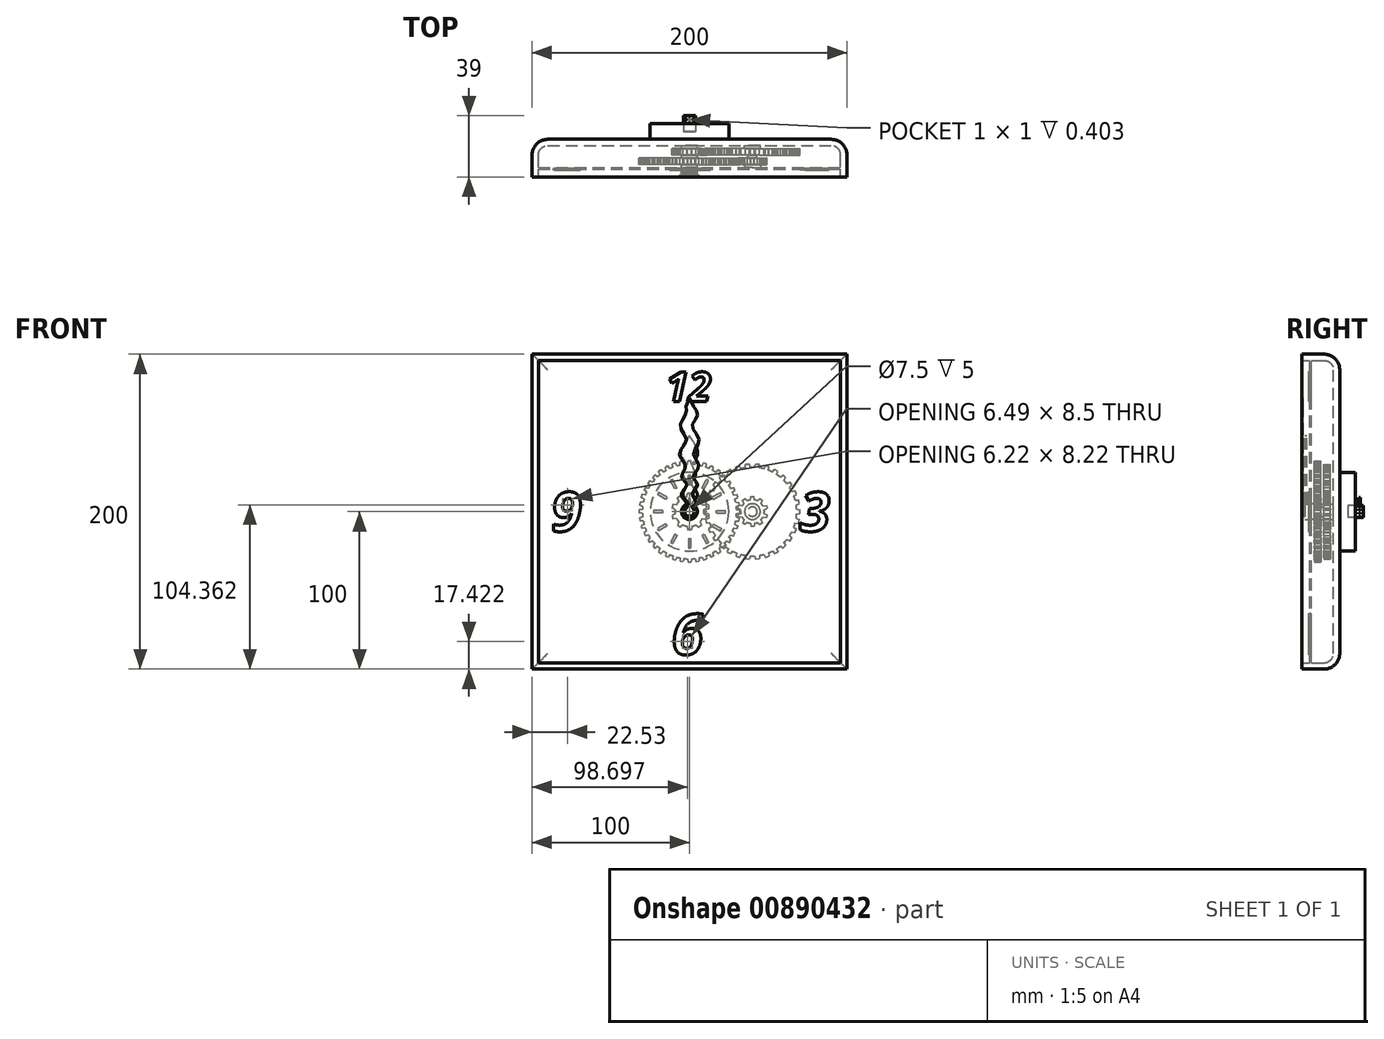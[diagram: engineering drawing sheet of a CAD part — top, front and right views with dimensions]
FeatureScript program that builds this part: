
annotation { "Feature Type Name" : "Feature", "Feature Type Description" : "" }
export const myFeature = defineFeature(function(context is Context, id is Id, definition is map)
    precondition{}
    {
        {
            var Q0;
            Q0=qCreatedBy(makeId("Front.planeOp"),FACE);
            var sketch = newSketch(context, id + "F0", { "sketchPlane" : qUnion([Q0])});
            skLineSegment(sketch, "E0.bottom", {"start": v(-100, -100) * mm, "end": v(100, -100) * mm});
            skLineSegment(sketch, "E0.top", {"start": v(-100, 100) * mm, "end": v(100, 100) * mm});
            skLineSegment(sketch, "E0.left", {"start": v(-100, -100) * mm, "end": v(-100, 100) * mm});
            skLineSegment(sketch, "E0.right", {"start": v(100, -100) * mm, "end": v(100, 100) * mm});
            skPoint(sketch, "E0.middle", {"position": v(0, 0) * mm});
            skSolve(sketch);
        }
        {
            var Q0;
            Q0 = qSketchRegion(id + "F0", true);
            extrude(context, id + "F1", {"entities" : qUnion([Q0]), "depth" : 24 * mm, "offsetDistance" : 25 * mm});
        }
        {
            var Q0;
            Q0=makeQuery(id+"F1.opExtrude","CAP_EDGE",EDGE,{"disambiguationData":[OSD([sQuery(id+"F0.wireOp",EDGE,"E0.top")])],"isStart":true});
            var Q1;
            Q1=makeQuery(id+"F1.opExtrude","CAP_EDGE",EDGE,{"disambiguationData":[OSD([sQuery(id+"F0.wireOp",EDGE,"E0.left")])],"isStart":true});
            var Q2;
            Q2=makeQuery(id+"F1.opExtrude","CAP_EDGE",EDGE,{"disambiguationData":[OSD([sQuery(id+"F0.wireOp",EDGE,"E0.bottom")])],"isStart":true});
            var Q3;
            Q3=makeQuery(id+"F1.opExtrude","CAP_EDGE",EDGE,{"disambiguationData":[OSD([sQuery(id+"F0.wireOp",EDGE,"E0.right")])],"isStart":true});
            fillet(context, id + "F2", {"entities" : qUnion([Q0, Q1, Q2, Q3]), "radius" : 10 * mm, "tangentPropagation" : true, "allowEdgeOverflow" : false});
        }
        {
            var Q0;
            Q0=makeQuery(id+"F1.opExtrude","CAP_FACE",FACE,{"disambiguationData":[OSD([sQuery(id+"F0.wireOp",EDGE,"E0.bottom"),sQuery(id+"F0.wireOp",EDGE,"E0.top"),sQuery(id+"F0.wireOp",EDGE,"E0.left"),sQuery(id+"F0.wireOp",EDGE,"E0.right")])],"isStart":false});
            shell(context, id + "F3", {"entities" : qUnion([Q0]), "thickness" : 4 * mm});
        }
        {
            var Q0;
            Q0=makeQuery(id+"F3.opShell","OFFSET_FACE",FACE,{"disambiguationData":[OSD([sQuery(id+"F0.wireOp",EDGE,"E0.bottom"),sQuery(id+"F0.wireOp",EDGE,"E0.top"),sQuery(id+"F0.wireOp",EDGE,"E0.left"),sQuery(id+"F0.wireOp",EDGE,"E0.right")])]});
            var sketch = newSketch(context, id + "F4", { "sketchPlane" : qUnion([Q0])});
            skCircle(sketch, "E1", {"center": v(0, 0) * mm, "radius": 3 * mm});
            skCircle(sketch, "E2", {"center": v(0, 0) * mm, "radius": 5 * mm});
            skCircle(sketch, "E3", {"center": v(40, 0) * mm, "radius": 3 * mm});
            skCircle(sketch, "E4", {"center": v(40, 0) * mm, "radius": 5 * mm});
            skSolve(sketch);
        }
        {
            var Q0;
            Q0 = qSketchRegion(id + "F4", true);
            extrude(context, id + "F5", {"entities" : qUnion([Q0]), "operationType" : NewBodyOperationType.ADD, "depth" : 2 * mm, "offsetDistance" : 25 * mm});
        }
        {
            var Q0;
            Q0=makeQuery(id+"F5.boolean.opBoolean","SPLIT",FACE,{"disambiguationData":[TD([makeQuery(id+"F5.opExtrude","SWEPT_FACE",FACE,{"disambiguationData":[OSD([sQuery(id+"F4.wireOp",EDGE,"E1")])]})])],"derivedFrom":makeQuery(id+"F3.opShell","OFFSET_FACE",FACE,{"disambiguationData":[OSD([sQuery(id+"F0.wireOp",EDGE,"E0.bottom"),sQuery(id+"F0.wireOp",EDGE,"E0.top"),sQuery(id+"F0.wireOp",EDGE,"E0.left"),sQuery(id+"F0.wireOp",EDGE,"E0.right")])]})});
            extrude(context, id + "F6", {"entities" : qUnion([Q0]), "depth" : 19 * mm, "offsetDistance" : 25 * mm});
        }
        {
            var Q0;
            Q0=makeQuery(id+"F5.boolean.opBoolean","SPLIT",FACE,{"disambiguationData":[TD([makeQuery(id+"F5.opExtrude","SWEPT_FACE",FACE,{"disambiguationData":[OSD([sQuery(id+"F4.wireOp",EDGE,"E3")])]})])],"derivedFrom":makeQuery(id+"F3.opShell","OFFSET_FACE",FACE,{"disambiguationData":[OSD([sQuery(id+"F0.wireOp",EDGE,"E0.bottom"),sQuery(id+"F0.wireOp",EDGE,"E0.top"),sQuery(id+"F0.wireOp",EDGE,"E0.left"),sQuery(id+"F0.wireOp",EDGE,"E0.right")])]})});
            extrude(context, id + "F7", {"entities" : qUnion([Q0]), "depth" : 8 * mm, "offsetDistance" : 25 * mm});
        }
        {
            var Q0;
            Q0=makeQuery(id+"F5.opExtrude","CAP_FACE",FACE,{"disambiguationData":[OSD([sQuery(id+"F4.wireOp",EDGE,"E1"),sQuery(id+"F4.wireOp",EDGE,"E2")])],"isStart":false});
            var sketch = newSketch(context, id + "F8", { "sketchPlane" : qUnion([Q0])});
            skCircle(sketch, "E5", {"center": v(0, 0) * mm, "radius": 9.38 * mm});
            skLineSegment(sketch, "E6", {"start": v(1.55, 9.25) * mm, "end": v(1.18, 11.38) * mm});
            skLineSegment(sketch, "E7", {"start": v(1.18, 11.38) * mm, "end": v(0, 11.38) * mm});
            skLineSegment(sketch, "E8.MirrorCS", {"start": v(-1.18, 11.38) * mm, "end": v(0, 11.38) * mm});
            skLineSegment(sketch, "E9.MirrorCS", {"start": v(-1.55, 9.25) * mm, "end": v(-1.18, 11.38) * mm});
            skLineSegment(sketch, "E10.1.0", {"start": v(-4.18, 8.4) * mm, "end": v(-5.73, 9.9) * mm});
            skLineSegment(sketch, "E10.1.1", {"start": v(-5.73, 9.9) * mm, "end": v(-6.69, 9.2) * mm});
            skLineSegment(sketch, "E10.1.2", {"start": v(-7.64, 8.51) * mm, "end": v(-6.69, 9.2) * mm});
            skLineSegment(sketch, "E10.1.3", {"start": v(-6.7, 6.57) * mm, "end": v(-7.64, 8.51) * mm});
            skLineSegment(sketch, "E10.2.0", {"start": v(-8.31, 4.33) * mm, "end": v(-10.45, 4.64) * mm});
            skLineSegment(sketch, "E10.2.1", {"start": v(-10.45, 4.64) * mm, "end": v(-10.82, 3.52) * mm});
            skLineSegment(sketch, "E10.2.2", {"start": v(-11.18, 2.4) * mm, "end": v(-10.82, 3.52) * mm});
            skLineSegment(sketch, "E10.2.3", {"start": v(-9.27, 1.38) * mm, "end": v(-11.18, 2.4) * mm});
            skLineSegment(sketch, "E11.1.3.0", {"start": v(-9.27, -1.38) * mm, "end": v(-11.18, -2.4) * mm});
            skLineSegment(sketch, "E11.3.3.0", {"start": v(-11.18, -2.4) * mm, "end": v(-10.82, -3.52) * mm});
            skLineSegment(sketch, "E11.6.3.0", {"start": v(-10.45, -4.64) * mm, "end": v(-10.82, -3.52) * mm});
            skLineSegment(sketch, "E11.9.3.0", {"start": v(-8.31, -4.33) * mm, "end": v(-10.45, -4.64) * mm});
            skLineSegment(sketch, "E11.1.4.0", {"start": v(-6.7, -6.57) * mm, "end": v(-7.64, -8.51) * mm});
            skLineSegment(sketch, "E11.3.4.0", {"start": v(-7.64, -8.51) * mm, "end": v(-6.69, -9.2) * mm});
            skLineSegment(sketch, "E11.6.4.0", {"start": v(-5.73, -9.9) * mm, "end": v(-6.69, -9.2) * mm});
            skLineSegment(sketch, "E11.9.4.0", {"start": v(-4.18, -8.4) * mm, "end": v(-5.73, -9.9) * mm});
            skLineSegment(sketch, "E11.1.5.0", {"start": v(-1.55, -9.25) * mm, "end": v(-1.18, -11.38) * mm});
            skLineSegment(sketch, "E11.3.5.0", {"start": v(-1.18, -11.38) * mm, "end": v(0, -11.38) * mm});
            skLineSegment(sketch, "E11.6.5.0", {"start": v(1.18, -11.38) * mm, "end": v(0, -11.38) * mm});
            skLineSegment(sketch, "E11.9.5.0", {"start": v(1.55, -9.25) * mm, "end": v(1.18, -11.38) * mm});
            skLineSegment(sketch, "E11.1.6.0", {"start": v(4.18, -8.4) * mm, "end": v(5.73, -9.9) * mm});
            skLineSegment(sketch, "E11.3.6.0", {"start": v(5.73, -9.9) * mm, "end": v(6.69, -9.2) * mm});
            skLineSegment(sketch, "E11.6.6.0", {"start": v(7.64, -8.51) * mm, "end": v(6.69, -9.2) * mm});
            skLineSegment(sketch, "E11.9.6.0", {"start": v(6.7, -6.57) * mm, "end": v(7.64, -8.51) * mm});
            skLineSegment(sketch, "E11.1.7.0", {"start": v(8.31, -4.33) * mm, "end": v(10.45, -4.64) * mm});
            skLineSegment(sketch, "E11.3.7.0", {"start": v(10.45, -4.64) * mm, "end": v(10.82, -3.52) * mm});
            skLineSegment(sketch, "E11.6.7.0", {"start": v(11.18, -2.4) * mm, "end": v(10.82, -3.52) * mm});
            skLineSegment(sketch, "E11.9.7.0", {"start": v(9.27, -1.38) * mm, "end": v(11.18, -2.4) * mm});
            skLineSegment(sketch, "E11.1.8.0", {"start": v(9.27, 1.38) * mm, "end": v(11.18, 2.4) * mm});
            skLineSegment(sketch, "E11.3.8.0", {"start": v(11.18, 2.4) * mm, "end": v(10.82, 3.52) * mm});
            skLineSegment(sketch, "E11.6.8.0", {"start": v(10.45, 4.64) * mm, "end": v(10.82, 3.52) * mm});
            skLineSegment(sketch, "E11.9.8.0", {"start": v(8.31, 4.33) * mm, "end": v(10.45, 4.64) * mm});
            skLineSegment(sketch, "E11.1.9.0", {"start": v(6.7, 6.57) * mm, "end": v(7.64, 8.51) * mm});
            skLineSegment(sketch, "E11.3.9.0", {"start": v(7.64, 8.51) * mm, "end": v(6.69, 9.2) * mm});
            skLineSegment(sketch, "E11.6.9.0", {"start": v(5.73, 9.9) * mm, "end": v(6.69, 9.2) * mm});
            skLineSegment(sketch, "E11.9.9.0", {"start": v(4.18, 8.4) * mm, "end": v(5.73, 9.9) * mm});
            skSolve(sketch);
        }
        {
            var Q0;
            Q0 = qSketchRegion(id + "F8", true);
            extrude(context, id + "F9", {"entities" : qUnion([Q0]), "operationType" : NewBodyOperationType.ADD, "depth" : 4 * mm, "offsetDistance" : 25 * mm});
        }
        {
            var Q0;
            Q0=makeQuery(id+"F5.opExtrude","CAP_FACE",FACE,{"disambiguationData":[OSD([sQuery(id+"F4.wireOp",EDGE,"E3"),sQuery(id+"F4.wireOp",EDGE,"E4")])],"isStart":false});
            var sketch = newSketch(context, id + "F10", { "sketchPlane" : qUnion([Q0])});
            skCircle(sketch, "E12", {"center": v(40, 0) * mm, "radius": 28.12 * mm});
            skLineSegment(sketch, "E13", {"start": v(11.92, 1.54) * mm, "end": v(9.88, 1.18) * mm});
            skLineSegment(sketch, "E14", {"start": v(9.88, 1.18) * mm, "end": v(9.88, 0) * mm});
            skLineSegment(sketch, "E15.MirrorCS", {"start": v(9.88, -1.18) * mm, "end": v(9.88, 0) * mm});
            skLineSegment(sketch, "E16.MirrorCS", {"start": v(11.92, -1.54) * mm, "end": v(9.88, -1.18) * mm});
            skLineSegment(sketch, "E17.1.0", {"start": v(12.21, -4.33) * mm, "end": v(10.29, -5.11) * mm});
            skLineSegment(sketch, "E17.1.1", {"start": v(10.29, -5.11) * mm, "end": v(10.53, -6.26) * mm});
            skLineSegment(sketch, "E17.1.2", {"start": v(10.78, -7.42) * mm, "end": v(10.53, -6.26) * mm});
            skLineSegment(sketch, "E17.1.3", {"start": v(12.85, -7.34) * mm, "end": v(10.78, -7.42) * mm});
            skLineSegment(sketch, "E17.2.0", {"start": v(13.72, -10.02) * mm, "end": v(12, -11.18) * mm});
            skLineSegment(sketch, "E17.2.1", {"start": v(12, -11.18) * mm, "end": v(12.48, -12.25) * mm});
            skLineSegment(sketch, "E17.2.2", {"start": v(12.96, -13.33) * mm, "end": v(12.48, -12.25) * mm});
            skLineSegment(sketch, "E17.2.3", {"start": v(14.97, -12.83) * mm, "end": v(12.96, -13.33) * mm});
            skLineSegment(sketch, "E18.2.3.0", {"start": v(16.38, -15.26) * mm, "end": v(14.94, -16.75) * mm});
            skLineSegment(sketch, "E18.3.3.0", {"start": v(14.94, -16.75) * mm, "end": v(15.63, -17.7) * mm});
            skLineSegment(sketch, "E18.6.3.0", {"start": v(16.32, -18.66) * mm, "end": v(15.63, -17.7) * mm});
            skLineSegment(sketch, "E18.9.3.0", {"start": v(18.18, -17.75) * mm, "end": v(16.32, -18.66) * mm});
            skLineSegment(sketch, "E18.2.4.0", {"start": v(20.07, -19.84) * mm, "end": v(18.97, -21.6) * mm});
            skLineSegment(sketch, "E18.3.4.0", {"start": v(18.97, -21.6) * mm, "end": v(19.84, -22.39) * mm});
            skLineSegment(sketch, "E18.6.4.0", {"start": v(20.72, -23.18) * mm, "end": v(19.84, -22.39) * mm});
            skLineSegment(sketch, "E18.9.4.0", {"start": v(22.35, -21.9) * mm, "end": v(20.72, -23.18) * mm});
            skLineSegment(sketch, "E18.2.5.0", {"start": v(24.63, -23.55) * mm, "end": v(23.92, -25.5) * mm});
            skLineSegment(sketch, "E18.3.5.0", {"start": v(23.92, -25.5) * mm, "end": v(24.94, -26.09) * mm});
            skLineSegment(sketch, "E18.6.5.0", {"start": v(25.96, -26.68) * mm, "end": v(24.94, -26.09) * mm});
            skLineSegment(sketch, "E18.9.5.0", {"start": v(27.3, -25.09) * mm, "end": v(25.96, -26.68) * mm});
            skLineSegment(sketch, "E18.2.6.0", {"start": v(29.86, -26.23) * mm, "end": v(29.57, -28.29) * mm});
            skLineSegment(sketch, "E18.3.6.0", {"start": v(29.57, -28.29) * mm, "end": v(30.7, -28.65) * mm});
            skLineSegment(sketch, "E18.6.6.0", {"start": v(31.81, -29.01) * mm, "end": v(30.7, -28.65) * mm});
            skLineSegment(sketch, "E18.9.6.0", {"start": v(32.78, -27.18) * mm, "end": v(31.81, -29.01) * mm});
            skLineSegment(sketch, "E18.2.7.0", {"start": v(35.53, -27.77) * mm, "end": v(35.68, -29.84) * mm});
            skLineSegment(sketch, "E18.3.7.0", {"start": v(35.68, -29.84) * mm, "end": v(36.85, -29.96) * mm});
            skLineSegment(sketch, "E18.6.7.0", {"start": v(38.02, -30.08) * mm, "end": v(36.85, -29.96) * mm});
            skLineSegment(sketch, "E18.9.7.0", {"start": v(38.6, -28.09) * mm, "end": v(38.02, -30.08) * mm});
            skLineSegment(sketch, "E18.2.8.0", {"start": v(41.4, -28.09) * mm, "end": v(41.98, -30.08) * mm});
            skLineSegment(sketch, "E18.3.8.0", {"start": v(41.98, -30.08) * mm, "end": v(43.15, -29.96) * mm});
            skLineSegment(sketch, "E18.6.8.0", {"start": v(44.32, -29.84) * mm, "end": v(43.15, -29.96) * mm});
            skLineSegment(sketch, "E18.9.8.0", {"start": v(44.47, -27.77) * mm, "end": v(44.32, -29.84) * mm});
            skLineSegment(sketch, "E18.2.9.0", {"start": v(47.22, -27.18) * mm, "end": v(48.19, -29.01) * mm});
            skLineSegment(sketch, "E18.3.9.0", {"start": v(48.19, -29.01) * mm, "end": v(49.3, -28.65) * mm});
            skLineSegment(sketch, "E18.6.9.0", {"start": v(50.43, -28.29) * mm, "end": v(49.3, -28.65) * mm});
            skLineSegment(sketch, "E18.9.9.0", {"start": v(50.14, -26.23) * mm, "end": v(50.43, -28.29) * mm});
            skLineSegment(sketch, "E18.2.10.0", {"start": v(52.7, -25.09) * mm, "end": v(54.04, -26.68) * mm});
            skLineSegment(sketch, "E18.3.10.0", {"start": v(54.04, -26.68) * mm, "end": v(55.06, -26.09) * mm});
            skLineSegment(sketch, "E18.6.10.0", {"start": v(56.08, -25.5) * mm, "end": v(55.06, -26.09) * mm});
            skLineSegment(sketch, "E18.9.10.0", {"start": v(55.37, -23.55) * mm, "end": v(56.08, -25.5) * mm});
            skLineSegment(sketch, "E18.2.11.0", {"start": v(57.65, -21.9) * mm, "end": v(59.28, -23.18) * mm});
            skLineSegment(sketch, "E18.3.11.0", {"start": v(59.28, -23.18) * mm, "end": v(60.16, -22.39) * mm});
            skLineSegment(sketch, "E18.6.11.0", {"start": v(61.03, -21.6) * mm, "end": v(60.16, -22.39) * mm});
            skLineSegment(sketch, "E18.9.11.0", {"start": v(59.93, -19.84) * mm, "end": v(61.03, -21.6) * mm});
            skLineSegment(sketch, "E18.2.12.0", {"start": v(61.82, -17.75) * mm, "end": v(63.68, -18.66) * mm});
            skLineSegment(sketch, "E18.3.12.0", {"start": v(63.68, -18.66) * mm, "end": v(64.37, -17.7) * mm});
            skLineSegment(sketch, "E18.6.12.0", {"start": v(65.06, -16.75) * mm, "end": v(64.37, -17.7) * mm});
            skLineSegment(sketch, "E18.9.12.0", {"start": v(63.62, -15.26) * mm, "end": v(65.06, -16.75) * mm});
            skLineSegment(sketch, "E18.2.13.0", {"start": v(65.03, -12.83) * mm, "end": v(67.04, -13.33) * mm});
            skLineSegment(sketch, "E18.3.13.0", {"start": v(67.04, -13.33) * mm, "end": v(67.52, -12.25) * mm});
            skLineSegment(sketch, "E18.6.13.0", {"start": v(68, -11.18) * mm, "end": v(67.52, -12.25) * mm});
            skLineSegment(sketch, "E18.9.13.0", {"start": v(66.28, -10.02) * mm, "end": v(68, -11.18) * mm});
            skLineSegment(sketch, "E18.2.14.0", {"start": v(67.15, -7.34) * mm, "end": v(69.22, -7.42) * mm});
            skLineSegment(sketch, "E18.3.14.0", {"start": v(69.22, -7.42) * mm, "end": v(69.47, -6.26) * mm});
            skLineSegment(sketch, "E18.6.14.0", {"start": v(69.71, -5.11) * mm, "end": v(69.47, -6.26) * mm});
            skLineSegment(sketch, "E18.9.14.0", {"start": v(67.79, -4.33) * mm, "end": v(69.71, -5.11) * mm});
            skLineSegment(sketch, "E18.2.15.0", {"start": v(68.08, -1.54) * mm, "end": v(70.12, -1.18) * mm});
            skLineSegment(sketch, "E18.3.15.0", {"start": v(70.12, -1.18) * mm, "end": v(70.12, 0) * mm});
            skLineSegment(sketch, "E18.6.15.0", {"start": v(70.12, 1.18) * mm, "end": v(70.12, 0) * mm});
            skLineSegment(sketch, "E18.9.15.0", {"start": v(68.08, 1.54) * mm, "end": v(70.12, 1.18) * mm});
            skLineSegment(sketch, "E18.2.16.0", {"start": v(67.79, 4.33) * mm, "end": v(69.71, 5.11) * mm});
            skLineSegment(sketch, "E18.3.16.0", {"start": v(69.71, 5.11) * mm, "end": v(69.47, 6.26) * mm});
            skLineSegment(sketch, "E18.6.16.0", {"start": v(69.22, 7.42) * mm, "end": v(69.47, 6.26) * mm});
            skLineSegment(sketch, "E18.9.16.0", {"start": v(67.15, 7.34) * mm, "end": v(69.22, 7.42) * mm});
            skLineSegment(sketch, "E18.2.17.0", {"start": v(66.28, 10.02) * mm, "end": v(68, 11.18) * mm});
            skLineSegment(sketch, "E18.3.17.0", {"start": v(68, 11.18) * mm, "end": v(67.52, 12.25) * mm});
            skLineSegment(sketch, "E18.6.17.0", {"start": v(67.04, 13.33) * mm, "end": v(67.52, 12.25) * mm});
            skLineSegment(sketch, "E18.9.17.0", {"start": v(65.03, 12.83) * mm, "end": v(67.04, 13.33) * mm});
            skLineSegment(sketch, "E18.2.18.0", {"start": v(63.62, 15.26) * mm, "end": v(65.06, 16.75) * mm});
            skLineSegment(sketch, "E18.3.18.0", {"start": v(65.06, 16.75) * mm, "end": v(64.37, 17.7) * mm});
            skLineSegment(sketch, "E18.6.18.0", {"start": v(63.68, 18.66) * mm, "end": v(64.37, 17.7) * mm});
            skLineSegment(sketch, "E18.9.18.0", {"start": v(61.82, 17.75) * mm, "end": v(63.68, 18.66) * mm});
            skLineSegment(sketch, "E18.2.19.0", {"start": v(59.93, 19.84) * mm, "end": v(61.03, 21.6) * mm});
            skLineSegment(sketch, "E18.3.19.0", {"start": v(61.03, 21.6) * mm, "end": v(60.16, 22.39) * mm});
            skLineSegment(sketch, "E18.6.19.0", {"start": v(59.28, 23.18) * mm, "end": v(60.16, 22.39) * mm});
            skLineSegment(sketch, "E18.9.19.0", {"start": v(57.65, 21.9) * mm, "end": v(59.28, 23.18) * mm});
            skLineSegment(sketch, "E18.2.20.0", {"start": v(55.37, 23.55) * mm, "end": v(56.08, 25.5) * mm});
            skLineSegment(sketch, "E18.3.20.0", {"start": v(56.08, 25.5) * mm, "end": v(55.06, 26.09) * mm});
            skLineSegment(sketch, "E18.6.20.0", {"start": v(54.04, 26.68) * mm, "end": v(55.06, 26.09) * mm});
            skLineSegment(sketch, "E18.9.20.0", {"start": v(52.7, 25.09) * mm, "end": v(54.04, 26.68) * mm});
            skLineSegment(sketch, "E18.2.21.0", {"start": v(50.14, 26.23) * mm, "end": v(50.43, 28.29) * mm});
            skLineSegment(sketch, "E18.3.21.0", {"start": v(50.43, 28.29) * mm, "end": v(49.3, 28.65) * mm});
            skLineSegment(sketch, "E18.6.21.0", {"start": v(48.19, 29.01) * mm, "end": v(49.3, 28.65) * mm});
            skLineSegment(sketch, "E18.9.21.0", {"start": v(47.22, 27.18) * mm, "end": v(48.19, 29.01) * mm});
            skLineSegment(sketch, "E18.2.22.0", {"start": v(44.47, 27.77) * mm, "end": v(44.32, 29.84) * mm});
            skLineSegment(sketch, "E18.3.22.0", {"start": v(44.32, 29.84) * mm, "end": v(43.15, 29.96) * mm});
            skLineSegment(sketch, "E18.6.22.0", {"start": v(41.98, 30.08) * mm, "end": v(43.15, 29.96) * mm});
            skLineSegment(sketch, "E18.9.22.0", {"start": v(41.4, 28.09) * mm, "end": v(41.98, 30.08) * mm});
            skLineSegment(sketch, "E18.2.23.0", {"start": v(38.6, 28.09) * mm, "end": v(38.02, 30.08) * mm});
            skLineSegment(sketch, "E18.3.23.0", {"start": v(38.02, 30.08) * mm, "end": v(36.85, 29.96) * mm});
            skLineSegment(sketch, "E18.6.23.0", {"start": v(35.68, 29.84) * mm, "end": v(36.85, 29.96) * mm});
            skLineSegment(sketch, "E18.9.23.0", {"start": v(35.53, 27.77) * mm, "end": v(35.68, 29.84) * mm});
            skLineSegment(sketch, "E18.2.24.0", {"start": v(32.78, 27.18) * mm, "end": v(31.81, 29.01) * mm});
            skLineSegment(sketch, "E18.3.24.0", {"start": v(31.81, 29.01) * mm, "end": v(30.7, 28.65) * mm});
            skLineSegment(sketch, "E18.6.24.0", {"start": v(29.57, 28.29) * mm, "end": v(30.7, 28.65) * mm});
            skLineSegment(sketch, "E18.9.24.0", {"start": v(29.86, 26.23) * mm, "end": v(29.57, 28.29) * mm});
            skLineSegment(sketch, "E18.2.25.0", {"start": v(27.3, 25.09) * mm, "end": v(25.96, 26.68) * mm});
            skLineSegment(sketch, "E18.3.25.0", {"start": v(25.96, 26.68) * mm, "end": v(24.94, 26.09) * mm});
            skLineSegment(sketch, "E18.6.25.0", {"start": v(23.92, 25.5) * mm, "end": v(24.94, 26.09) * mm});
            skLineSegment(sketch, "E18.9.25.0", {"start": v(24.63, 23.55) * mm, "end": v(23.92, 25.5) * mm});
            skLineSegment(sketch, "E18.2.26.0", {"start": v(22.35, 21.9) * mm, "end": v(20.72, 23.18) * mm});
            skLineSegment(sketch, "E18.3.26.0", {"start": v(20.72, 23.18) * mm, "end": v(19.84, 22.39) * mm});
            skLineSegment(sketch, "E18.6.26.0", {"start": v(18.97, 21.6) * mm, "end": v(19.84, 22.39) * mm});
            skLineSegment(sketch, "E18.9.26.0", {"start": v(20.07, 19.84) * mm, "end": v(18.97, 21.6) * mm});
            skLineSegment(sketch, "E18.2.27.0", {"start": v(18.18, 17.75) * mm, "end": v(16.32, 18.66) * mm});
            skLineSegment(sketch, "E18.3.27.0", {"start": v(16.32, 18.66) * mm, "end": v(15.63, 17.7) * mm});
            skLineSegment(sketch, "E18.6.27.0", {"start": v(14.94, 16.75) * mm, "end": v(15.63, 17.7) * mm});
            skLineSegment(sketch, "E18.9.27.0", {"start": v(16.38, 15.26) * mm, "end": v(14.94, 16.75) * mm});
            skLineSegment(sketch, "E18.2.28.0", {"start": v(14.97, 12.83) * mm, "end": v(12.96, 13.33) * mm});
            skLineSegment(sketch, "E18.3.28.0", {"start": v(12.96, 13.33) * mm, "end": v(12.48, 12.25) * mm});
            skLineSegment(sketch, "E18.6.28.0", {"start": v(12, 11.18) * mm, "end": v(12.48, 12.25) * mm});
            skLineSegment(sketch, "E18.9.28.0", {"start": v(13.72, 10.02) * mm, "end": v(12, 11.18) * mm});
            skLineSegment(sketch, "E18.2.29.0", {"start": v(12.85, 7.34) * mm, "end": v(10.78, 7.42) * mm});
            skLineSegment(sketch, "E18.3.29.0", {"start": v(10.78, 7.42) * mm, "end": v(10.53, 6.26) * mm});
            skLineSegment(sketch, "E18.6.29.0", {"start": v(10.29, 5.11) * mm, "end": v(10.53, 6.26) * mm});
            skLineSegment(sketch, "E18.9.29.0", {"start": v(12.21, 4.33) * mm, "end": v(10.29, 5.11) * mm});
            skSolve(sketch);
        }
        {
            var Q0;
            Q0 = qSketchRegion(id + "F10", true);
            extrude(context, id + "F11", {"entities" : qUnion([Q0]), "operationType" : NewBodyOperationType.ADD, "depth" : 4 * mm, "offsetDistance" : 25 * mm});
        }
        {
            var Q0;
            Q0=makeQuery(id+"F9.opExtrude","CAP_FACE",FACE,{"disambiguationData":[OSD([sQuery(id+"F8.wireOp",EDGE,"E5"),sQuery(id+"F8.wireOp",EDGE,"E6"),sQuery(id+"F8.wireOp",EDGE,"E7"),sQuery(id+"F8.wireOp",EDGE,"E8.MirrorCS"),sQuery(id+"F8.wireOp",EDGE,"E9.MirrorCS"),sQuery(id+"F8.wireOp",EDGE,"E10.1.0"),sQuery(id+"F8.wireOp",EDGE,"E10.1.1"),sQuery(id+"F8.wireOp",EDGE,"E10.1.2"),sQuery(id+"F8.wireOp",EDGE,"E10.1.3"),sQuery(id+"F8.wireOp",EDGE,"E10.2.0"),sQuery(id+"F8.wireOp",EDGE,"E10.2.1"),sQuery(id+"F8.wireOp",EDGE,"E10.2.2"),sQuery(id+"F8.wireOp",EDGE,"E10.2.3"),sQuery(id+"F8.wireOp",EDGE,"E11.1.3.0"),sQuery(id+"F8.wireOp",EDGE,"E11.3.3.0"),sQuery(id+"F8.wireOp",EDGE,"E11.6.3.0"),sQuery(id+"F8.wireOp",EDGE,"E11.9.3.0"),sQuery(id+"F8.wireOp",EDGE,"E11.1.4.0"),sQuery(id+"F8.wireOp",EDGE,"E11.3.4.0"),sQuery(id+"F8.wireOp",EDGE,"E11.6.4.0"),sQuery(id+"F8.wireOp",EDGE,"E11.9.4.0"),sQuery(id+"F8.wireOp",EDGE,"E11.1.5.0"),sQuery(id+"F8.wireOp",EDGE,"E11.3.5.0"),sQuery(id+"F8.wireOp",EDGE,"E11.6.5.0"),sQuery(id+"F8.wireOp",EDGE,"E11.9.5.0"),sQuery(id+"F8.wireOp",EDGE,"E11.1.6.0"),sQuery(id+"F8.wireOp",EDGE,"E11.3.6.0"),sQuery(id+"F8.wireOp",EDGE,"E11.6.6.0"),sQuery(id+"F8.wireOp",EDGE,"E11.9.6.0"),sQuery(id+"F8.wireOp",EDGE,"E11.1.7.0"),sQuery(id+"F8.wireOp",EDGE,"E11.3.7.0"),sQuery(id+"F8.wireOp",EDGE,"E11.6.7.0"),sQuery(id+"F8.wireOp",EDGE,"E11.9.7.0"),sQuery(id+"F8.wireOp",EDGE,"E11.1.8.0"),sQuery(id+"F8.wireOp",EDGE,"E11.3.8.0"),sQuery(id+"F8.wireOp",EDGE,"E11.6.8.0"),sQuery(id+"F8.wireOp",EDGE,"E11.9.8.0"),sQuery(id+"F8.wireOp",EDGE,"E11.1.9.0"),sQuery(id+"F8.wireOp",EDGE,"E11.3.9.0"),sQuery(id+"F8.wireOp",EDGE,"E11.6.9.0"),sQuery(id+"F8.wireOp",EDGE,"E11.9.9.0")])],"isStart":false});
            var sketch = newSketch(context, id + "F12", { "sketchPlane" : qUnion([Q0])});
            skCircle(sketch, "E19.0", {"center": v(0, 0) * mm, "radius": 3 * mm});
            skCircle(sketch, "E20.0", {"center": v(0, 0) * mm, "radius": 5 * mm});
            skSolve(sketch);
        }
        {
            var Q0;
            Q0 = qSketchRegion(id + "F12", true);
            extrude(context, id + "F13", {"entities" : qUnion([Q0]), "depth" : 2 * mm, "offsetDistance" : 25 * mm});
        }
        {
            var Q0;
            Q0=makeQuery(id+"F13.opExtrude","CAP_FACE",FACE,{"disambiguationData":[OSD([sQuery(id+"F12.wireOp",EDGE,"E19.0"),sQuery(id+"F12.wireOp",EDGE,"E20.0")])],"isStart":false});
            var sketch = newSketch(context, id + "F14", { "sketchPlane" : qUnion([Q0])});
            skCircle(sketch, "E21.0", {"center": v(0, 0) * mm, "radius": 3 * mm});
            skCircle(sketch, "E22", {"center": v(0, 0) * mm, "radius": 30 * mm});
            skLineSegment(sketch, "E23", {"start": v(1.3, 29.97) * mm, "end": v(0.94, 32) * mm});
            skLineSegment(sketch, "E24", {"start": v(0.94, 32) * mm, "end": v(0, 32) * mm});
            skLineSegment(sketch, "E25.MirrorCS", {"start": v(-0.94, 32) * mm, "end": v(0, 32) * mm});
            skLineSegment(sketch, "E26.MirrorCS", {"start": v(-1.3, 29.97) * mm, "end": v(-0.94, 32) * mm});
            skLineSegment(sketch, "E27.1.0", {"start": v(-3.4, 29.8) * mm, "end": v(-4.08, 31.75) * mm});
            skLineSegment(sketch, "E27.1.1", {"start": v(-4.08, 31.75) * mm, "end": v(-5, 31.6) * mm});
            skLineSegment(sketch, "E27.1.2", {"start": v(-5.94, 31.46) * mm, "end": v(-5, 31.6) * mm});
            skLineSegment(sketch, "E27.1.3", {"start": v(-5.97, 29.4) * mm, "end": v(-5.94, 31.46) * mm});
            skLineSegment(sketch, "E27.2.0", {"start": v(-8.03, 28.9) * mm, "end": v(-9, 30.73) * mm});
            skLineSegment(sketch, "E27.2.1", {"start": v(-9, 30.73) * mm, "end": v(-9.89, 30.43) * mm});
            skLineSegment(sketch, "E27.2.2", {"start": v(-10.78, 30.14) * mm, "end": v(-9.89, 30.43) * mm});
            skLineSegment(sketch, "E27.2.3", {"start": v(-10.5, 28.1) * mm, "end": v(-10.78, 30.14) * mm});
            skLineSegment(sketch, "E28.1.3.0", {"start": v(-12.45, 27.3) * mm, "end": v(-13.69, 28.94) * mm});
            skLineSegment(sketch, "E28.3.3.0", {"start": v(-13.69, 28.94) * mm, "end": v(-14.53, 28.51) * mm});
            skLineSegment(sketch, "E28.6.3.0", {"start": v(-15.37, 28.08) * mm, "end": v(-14.53, 28.51) * mm});
            skLineSegment(sketch, "E28.9.3.0", {"start": v(-14.77, 26.11) * mm, "end": v(-15.37, 28.08) * mm});
            skLineSegment(sketch, "E28.1.4.0", {"start": v(-16.57, 25.01) * mm, "end": v(-18.05, 26.44) * mm});
            skLineSegment(sketch, "E28.3.4.0", {"start": v(-18.05, 26.44) * mm, "end": v(-18.8, 25.89) * mm});
            skLineSegment(sketch, "E28.6.4.0", {"start": v(-19.57, 25.33) * mm, "end": v(-18.8, 25.89) * mm});
            skLineSegment(sketch, "E28.9.4.0", {"start": v(-18.67, 23.48) * mm, "end": v(-19.57, 25.33) * mm});
            skLineSegment(sketch, "E28.1.5.0", {"start": v(-20.27, 22.11) * mm, "end": v(-21.96, 23.3) * mm});
            skLineSegment(sketch, "E28.3.5.0", {"start": v(-21.96, 23.3) * mm, "end": v(-22.63, 22.63) * mm});
            skLineSegment(sketch, "E28.6.5.0", {"start": v(-23.3, 21.96) * mm, "end": v(-22.63, 22.63) * mm});
            skLineSegment(sketch, "E28.9.5.0", {"start": v(-22.11, 20.27) * mm, "end": v(-23.3, 21.96) * mm});
            skLineSegment(sketch, "E28.1.6.0", {"start": v(-23.48, 18.67) * mm, "end": v(-25.33, 19.57) * mm});
            skLineSegment(sketch, "E28.3.6.0", {"start": v(-25.33, 19.57) * mm, "end": v(-25.89, 18.8) * mm});
            skLineSegment(sketch, "E28.6.6.0", {"start": v(-26.44, 18.05) * mm, "end": v(-25.89, 18.8) * mm});
            skLineSegment(sketch, "E28.9.6.0", {"start": v(-25.01, 16.57) * mm, "end": v(-26.44, 18.05) * mm});
            skLineSegment(sketch, "E28.1.7.0", {"start": v(-26.11, 14.77) * mm, "end": v(-28.08, 15.37) * mm});
            skLineSegment(sketch, "E28.3.7.0", {"start": v(-28.08, 15.37) * mm, "end": v(-28.51, 14.53) * mm});
            skLineSegment(sketch, "E28.6.7.0", {"start": v(-28.94, 13.69) * mm, "end": v(-28.51, 14.53) * mm});
            skLineSegment(sketch, "E28.9.7.0", {"start": v(-27.3, 12.45) * mm, "end": v(-28.94, 13.69) * mm});
            skLineSegment(sketch, "E28.1.8.0", {"start": v(-28.1, 10.5) * mm, "end": v(-30.14, 10.78) * mm});
            skLineSegment(sketch, "E28.3.8.0", {"start": v(-30.14, 10.78) * mm, "end": v(-30.43, 9.89) * mm});
            skLineSegment(sketch, "E28.6.8.0", {"start": v(-30.73, 9) * mm, "end": v(-30.43, 9.89) * mm});
            skLineSegment(sketch, "E28.9.8.0", {"start": v(-28.9, 8.03) * mm, "end": v(-30.73, 9) * mm});
            skLineSegment(sketch, "E28.1.9.0", {"start": v(-29.4, 5.97) * mm, "end": v(-31.46, 5.94) * mm});
            skLineSegment(sketch, "E28.3.9.0", {"start": v(-31.46, 5.94) * mm, "end": v(-31.6, 5) * mm});
            skLineSegment(sketch, "E28.6.9.0", {"start": v(-31.75, 4.08) * mm, "end": v(-31.6, 5) * mm});
            skLineSegment(sketch, "E28.9.9.0", {"start": v(-29.8, 3.4) * mm, "end": v(-31.75, 4.08) * mm});
            skLineSegment(sketch, "E28.1.10.0", {"start": v(-29.97, 1.3) * mm, "end": v(-32, 0.94) * mm});
            skLineSegment(sketch, "E28.3.10.0", {"start": v(-32, 0.94) * mm, "end": v(-32, 0) * mm});
            skLineSegment(sketch, "E28.6.10.0", {"start": v(-32, -0.94) * mm, "end": v(-32, 0) * mm});
            skLineSegment(sketch, "E28.9.10.0", {"start": v(-29.97, -1.3) * mm, "end": v(-32, -0.94) * mm});
            skLineSegment(sketch, "E28.1.11.0", {"start": v(-29.8, -3.4) * mm, "end": v(-31.75, -4.08) * mm});
            skLineSegment(sketch, "E28.3.11.0", {"start": v(-31.75, -4.08) * mm, "end": v(-31.6, -5) * mm});
            skLineSegment(sketch, "E28.6.11.0", {"start": v(-31.46, -5.94) * mm, "end": v(-31.6, -5) * mm});
            skLineSegment(sketch, "E28.9.11.0", {"start": v(-29.4, -5.97) * mm, "end": v(-31.46, -5.94) * mm});
            skLineSegment(sketch, "E28.1.12.0", {"start": v(-28.9, -8.03) * mm, "end": v(-30.73, -9) * mm});
            skLineSegment(sketch, "E28.3.12.0", {"start": v(-30.73, -9) * mm, "end": v(-30.43, -9.89) * mm});
            skLineSegment(sketch, "E28.6.12.0", {"start": v(-30.14, -10.78) * mm, "end": v(-30.43, -9.89) * mm});
            skLineSegment(sketch, "E28.9.12.0", {"start": v(-28.1, -10.5) * mm, "end": v(-30.14, -10.78) * mm});
            skLineSegment(sketch, "E28.1.13.0", {"start": v(-27.3, -12.45) * mm, "end": v(-28.94, -13.69) * mm});
            skLineSegment(sketch, "E28.3.13.0", {"start": v(-28.94, -13.69) * mm, "end": v(-28.51, -14.53) * mm});
            skLineSegment(sketch, "E28.6.13.0", {"start": v(-28.08, -15.37) * mm, "end": v(-28.51, -14.53) * mm});
            skLineSegment(sketch, "E28.9.13.0", {"start": v(-26.11, -14.77) * mm, "end": v(-28.08, -15.37) * mm});
            skLineSegment(sketch, "E28.1.14.0", {"start": v(-25.01, -16.57) * mm, "end": v(-26.44, -18.05) * mm});
            skLineSegment(sketch, "E28.3.14.0", {"start": v(-26.44, -18.05) * mm, "end": v(-25.89, -18.8) * mm});
            skLineSegment(sketch, "E28.6.14.0", {"start": v(-25.33, -19.57) * mm, "end": v(-25.89, -18.8) * mm});
            skLineSegment(sketch, "E28.9.14.0", {"start": v(-23.48, -18.67) * mm, "end": v(-25.33, -19.57) * mm});
            skLineSegment(sketch, "E28.1.15.0", {"start": v(-22.11, -20.27) * mm, "end": v(-23.3, -21.96) * mm});
            skLineSegment(sketch, "E28.3.15.0", {"start": v(-23.3, -21.96) * mm, "end": v(-22.63, -22.63) * mm});
            skLineSegment(sketch, "E28.6.15.0", {"start": v(-21.96, -23.3) * mm, "end": v(-22.63, -22.63) * mm});
            skLineSegment(sketch, "E28.9.15.0", {"start": v(-20.27, -22.11) * mm, "end": v(-21.96, -23.3) * mm});
            skLineSegment(sketch, "E28.1.16.0", {"start": v(-18.67, -23.48) * mm, "end": v(-19.57, -25.33) * mm});
            skLineSegment(sketch, "E28.3.16.0", {"start": v(-19.57, -25.33) * mm, "end": v(-18.8, -25.89) * mm});
            skLineSegment(sketch, "E28.6.16.0", {"start": v(-18.05, -26.44) * mm, "end": v(-18.8, -25.89) * mm});
            skLineSegment(sketch, "E28.9.16.0", {"start": v(-16.57, -25.01) * mm, "end": v(-18.05, -26.44) * mm});
            skLineSegment(sketch, "E28.1.17.0", {"start": v(-14.77, -26.11) * mm, "end": v(-15.37, -28.08) * mm});
            skLineSegment(sketch, "E28.3.17.0", {"start": v(-15.37, -28.08) * mm, "end": v(-14.53, -28.51) * mm});
            skLineSegment(sketch, "E28.6.17.0", {"start": v(-13.69, -28.94) * mm, "end": v(-14.53, -28.51) * mm});
            skLineSegment(sketch, "E28.9.17.0", {"start": v(-12.45, -27.3) * mm, "end": v(-13.69, -28.94) * mm});
            skLineSegment(sketch, "E28.1.18.0", {"start": v(-10.5, -28.1) * mm, "end": v(-10.78, -30.14) * mm});
            skLineSegment(sketch, "E28.3.18.0", {"start": v(-10.78, -30.14) * mm, "end": v(-9.89, -30.43) * mm});
            skLineSegment(sketch, "E28.6.18.0", {"start": v(-9, -30.73) * mm, "end": v(-9.89, -30.43) * mm});
            skLineSegment(sketch, "E28.9.18.0", {"start": v(-8.03, -28.9) * mm, "end": v(-9, -30.73) * mm});
            skLineSegment(sketch, "E28.1.19.0", {"start": v(-5.97, -29.4) * mm, "end": v(-5.94, -31.46) * mm});
            skLineSegment(sketch, "E28.3.19.0", {"start": v(-5.94, -31.46) * mm, "end": v(-5, -31.6) * mm});
            skLineSegment(sketch, "E28.6.19.0", {"start": v(-4.08, -31.75) * mm, "end": v(-5, -31.6) * mm});
            skLineSegment(sketch, "E28.9.19.0", {"start": v(-3.4, -29.8) * mm, "end": v(-4.08, -31.75) * mm});
            skLineSegment(sketch, "E28.1.20.0", {"start": v(-1.3, -29.97) * mm, "end": v(-0.94, -32) * mm});
            skLineSegment(sketch, "E28.3.20.0", {"start": v(-0.94, -32) * mm, "end": v(0, -32) * mm});
            skLineSegment(sketch, "E28.6.20.0", {"start": v(0.94, -32) * mm, "end": v(0, -32) * mm});
            skLineSegment(sketch, "E28.9.20.0", {"start": v(1.3, -29.97) * mm, "end": v(0.94, -32) * mm});
            skLineSegment(sketch, "E28.1.21.0", {"start": v(3.4, -29.8) * mm, "end": v(4.08, -31.75) * mm});
            skLineSegment(sketch, "E28.3.21.0", {"start": v(4.08, -31.75) * mm, "end": v(5, -31.6) * mm});
            skLineSegment(sketch, "E28.6.21.0", {"start": v(5.94, -31.46) * mm, "end": v(5, -31.6) * mm});
            skLineSegment(sketch, "E28.9.21.0", {"start": v(5.97, -29.4) * mm, "end": v(5.94, -31.46) * mm});
            skLineSegment(sketch, "E28.1.22.0", {"start": v(8.03, -28.9) * mm, "end": v(9, -30.73) * mm});
            skLineSegment(sketch, "E28.3.22.0", {"start": v(9, -30.73) * mm, "end": v(9.89, -30.43) * mm});
            skLineSegment(sketch, "E28.6.22.0", {"start": v(10.78, -30.14) * mm, "end": v(9.89, -30.43) * mm});
            skLineSegment(sketch, "E28.9.22.0", {"start": v(10.5, -28.1) * mm, "end": v(10.78, -30.14) * mm});
            skLineSegment(sketch, "E28.1.23.0", {"start": v(12.45, -27.3) * mm, "end": v(13.69, -28.94) * mm});
            skLineSegment(sketch, "E28.3.23.0", {"start": v(13.69, -28.94) * mm, "end": v(14.53, -28.51) * mm});
            skLineSegment(sketch, "E28.6.23.0", {"start": v(15.37, -28.08) * mm, "end": v(14.53, -28.51) * mm});
            skLineSegment(sketch, "E28.9.23.0", {"start": v(14.77, -26.11) * mm, "end": v(15.37, -28.08) * mm});
            skLineSegment(sketch, "E28.1.24.0", {"start": v(16.57, -25.01) * mm, "end": v(18.05, -26.44) * mm});
            skLineSegment(sketch, "E28.3.24.0", {"start": v(18.05, -26.44) * mm, "end": v(18.8, -25.89) * mm});
            skLineSegment(sketch, "E28.6.24.0", {"start": v(19.57, -25.33) * mm, "end": v(18.8, -25.89) * mm});
            skLineSegment(sketch, "E28.9.24.0", {"start": v(18.67, -23.48) * mm, "end": v(19.57, -25.33) * mm});
            skLineSegment(sketch, "E28.1.25.0", {"start": v(20.27, -22.11) * mm, "end": v(21.96, -23.3) * mm});
            skLineSegment(sketch, "E28.3.25.0", {"start": v(21.96, -23.3) * mm, "end": v(22.63, -22.63) * mm});
            skLineSegment(sketch, "E28.6.25.0", {"start": v(23.3, -21.96) * mm, "end": v(22.63, -22.63) * mm});
            skLineSegment(sketch, "E28.9.25.0", {"start": v(22.11, -20.27) * mm, "end": v(23.3, -21.96) * mm});
            skLineSegment(sketch, "E28.1.26.0", {"start": v(23.48, -18.67) * mm, "end": v(25.33, -19.57) * mm});
            skLineSegment(sketch, "E28.3.26.0", {"start": v(25.33, -19.57) * mm, "end": v(25.89, -18.8) * mm});
            skLineSegment(sketch, "E28.6.26.0", {"start": v(26.44, -18.05) * mm, "end": v(25.89, -18.8) * mm});
            skLineSegment(sketch, "E28.9.26.0", {"start": v(25.01, -16.57) * mm, "end": v(26.44, -18.05) * mm});
            skLineSegment(sketch, "E28.1.27.0", {"start": v(26.11, -14.77) * mm, "end": v(28.08, -15.37) * mm});
            skLineSegment(sketch, "E28.3.27.0", {"start": v(28.08, -15.37) * mm, "end": v(28.51, -14.53) * mm});
            skLineSegment(sketch, "E28.6.27.0", {"start": v(28.94, -13.69) * mm, "end": v(28.51, -14.53) * mm});
            skLineSegment(sketch, "E28.9.27.0", {"start": v(27.3, -12.45) * mm, "end": v(28.94, -13.69) * mm});
            skLineSegment(sketch, "E28.1.28.0", {"start": v(28.1, -10.5) * mm, "end": v(30.14, -10.78) * mm});
            skLineSegment(sketch, "E28.3.28.0", {"start": v(30.14, -10.78) * mm, "end": v(30.43, -9.89) * mm});
            skLineSegment(sketch, "E28.6.28.0", {"start": v(30.73, -9) * mm, "end": v(30.43, -9.89) * mm});
            skLineSegment(sketch, "E28.9.28.0", {"start": v(28.9, -8.03) * mm, "end": v(30.73, -9) * mm});
            skLineSegment(sketch, "E28.1.29.0", {"start": v(29.4, -5.97) * mm, "end": v(31.46, -5.94) * mm});
            skLineSegment(sketch, "E28.3.29.0", {"start": v(31.46, -5.94) * mm, "end": v(31.6, -5) * mm});
            skLineSegment(sketch, "E28.6.29.0", {"start": v(31.75, -4.08) * mm, "end": v(31.6, -5) * mm});
            skLineSegment(sketch, "E28.9.29.0", {"start": v(29.8, -3.4) * mm, "end": v(31.75, -4.08) * mm});
            skLineSegment(sketch, "E28.1.30.0", {"start": v(29.97, -1.3) * mm, "end": v(32, -0.94) * mm});
            skLineSegment(sketch, "E28.3.30.0", {"start": v(32, -0.94) * mm, "end": v(32, 0) * mm});
            skLineSegment(sketch, "E28.6.30.0", {"start": v(32, 0.94) * mm, "end": v(32, 0) * mm});
            skLineSegment(sketch, "E28.9.30.0", {"start": v(29.97, 1.3) * mm, "end": v(32, 0.94) * mm});
            skLineSegment(sketch, "E28.1.31.0", {"start": v(29.8, 3.4) * mm, "end": v(31.75, 4.08) * mm});
            skLineSegment(sketch, "E28.3.31.0", {"start": v(31.75, 4.08) * mm, "end": v(31.6, 5) * mm});
            skLineSegment(sketch, "E28.6.31.0", {"start": v(31.46, 5.94) * mm, "end": v(31.6, 5) * mm});
            skLineSegment(sketch, "E28.9.31.0", {"start": v(29.4, 5.97) * mm, "end": v(31.46, 5.94) * mm});
            skLineSegment(sketch, "E28.1.32.0", {"start": v(28.9, 8.03) * mm, "end": v(30.73, 9) * mm});
            skLineSegment(sketch, "E28.3.32.0", {"start": v(30.73, 9) * mm, "end": v(30.43, 9.89) * mm});
            skLineSegment(sketch, "E28.6.32.0", {"start": v(30.14, 10.78) * mm, "end": v(30.43, 9.89) * mm});
            skLineSegment(sketch, "E28.9.32.0", {"start": v(28.1, 10.5) * mm, "end": v(30.14, 10.78) * mm});
            skLineSegment(sketch, "E28.1.33.0", {"start": v(27.3, 12.45) * mm, "end": v(28.94, 13.69) * mm});
            skLineSegment(sketch, "E28.3.33.0", {"start": v(28.94, 13.69) * mm, "end": v(28.51, 14.53) * mm});
            skLineSegment(sketch, "E28.6.33.0", {"start": v(28.08, 15.37) * mm, "end": v(28.51, 14.53) * mm});
            skLineSegment(sketch, "E28.9.33.0", {"start": v(26.11, 14.77) * mm, "end": v(28.08, 15.37) * mm});
            skLineSegment(sketch, "E28.1.34.0", {"start": v(25.01, 16.57) * mm, "end": v(26.44, 18.05) * mm});
            skLineSegment(sketch, "E28.3.34.0", {"start": v(26.44, 18.05) * mm, "end": v(25.89, 18.8) * mm});
            skLineSegment(sketch, "E28.6.34.0", {"start": v(25.33, 19.57) * mm, "end": v(25.89, 18.8) * mm});
            skLineSegment(sketch, "E28.9.34.0", {"start": v(23.48, 18.67) * mm, "end": v(25.33, 19.57) * mm});
            skLineSegment(sketch, "E28.1.35.0", {"start": v(22.11, 20.27) * mm, "end": v(23.3, 21.96) * mm});
            skLineSegment(sketch, "E28.3.35.0", {"start": v(23.3, 21.96) * mm, "end": v(22.63, 22.63) * mm});
            skLineSegment(sketch, "E28.6.35.0", {"start": v(21.96, 23.3) * mm, "end": v(22.63, 22.63) * mm});
            skLineSegment(sketch, "E28.9.35.0", {"start": v(20.27, 22.11) * mm, "end": v(21.96, 23.3) * mm});
            skLineSegment(sketch, "E28.1.36.0", {"start": v(18.67, 23.48) * mm, "end": v(19.57, 25.33) * mm});
            skLineSegment(sketch, "E28.3.36.0", {"start": v(19.57, 25.33) * mm, "end": v(18.8, 25.89) * mm});
            skLineSegment(sketch, "E28.6.36.0", {"start": v(18.05, 26.44) * mm, "end": v(18.8, 25.89) * mm});
            skLineSegment(sketch, "E28.9.36.0", {"start": v(16.57, 25.01) * mm, "end": v(18.05, 26.44) * mm});
            skLineSegment(sketch, "E28.1.37.0", {"start": v(14.77, 26.11) * mm, "end": v(15.37, 28.08) * mm});
            skLineSegment(sketch, "E28.3.37.0", {"start": v(15.37, 28.08) * mm, "end": v(14.53, 28.51) * mm});
            skLineSegment(sketch, "E28.6.37.0", {"start": v(13.69, 28.94) * mm, "end": v(14.53, 28.51) * mm});
            skLineSegment(sketch, "E28.9.37.0", {"start": v(12.45, 27.3) * mm, "end": v(13.69, 28.94) * mm});
            skLineSegment(sketch, "E28.1.38.0", {"start": v(10.5, 28.1) * mm, "end": v(10.78, 30.14) * mm});
            skLineSegment(sketch, "E28.3.38.0", {"start": v(10.78, 30.14) * mm, "end": v(9.89, 30.43) * mm});
            skLineSegment(sketch, "E28.6.38.0", {"start": v(9, 30.73) * mm, "end": v(9.89, 30.43) * mm});
            skLineSegment(sketch, "E28.9.38.0", {"start": v(8.03, 28.9) * mm, "end": v(9, 30.73) * mm});
            skLineSegment(sketch, "E28.1.39.0", {"start": v(5.97, 29.4) * mm, "end": v(5.94, 31.46) * mm});
            skLineSegment(sketch, "E28.3.39.0", {"start": v(5.94, 31.46) * mm, "end": v(5, 31.6) * mm});
            skLineSegment(sketch, "E28.6.39.0", {"start": v(4.08, 31.75) * mm, "end": v(5, 31.6) * mm});
            skLineSegment(sketch, "E28.9.39.0", {"start": v(3.4, 29.8) * mm, "end": v(4.08, 31.75) * mm});
            skSolve(sketch);
        }
        {
            var Q0;
            Q0 = qSketchRegion(id + "F14", true);
            extrude(context, id + "F15", {"entities" : qUnion([Q0]), "operationType" : NewBodyOperationType.ADD, "depth" : 4 * mm, "offsetDistance" : 25 * mm});
        }
        {
            var Q0;
            Q0=makeQuery(id+"F7.opExtrude","CAP_FACE",FACE,{"disambiguationData":[OSD([sQuery(id+"F0.wireOp",EDGE,"E0.bottom"),sQuery(id+"F0.wireOp",EDGE,"E0.top"),sQuery(id+"F0.wireOp",EDGE,"E0.left"),sQuery(id+"F0.wireOp",EDGE,"E0.right")])],"isStart":false});
            var sketch = newSketch(context, id + "F16", { "sketchPlane" : qUnion([Q0])});
            skCircle(sketch, "E29", {"center": v(40, 0) * mm, "radius": 7.5 * mm});
            skLineSegment(sketch, "E30", {"start": v(40, 0) * mm, "end": v(40, 7.5) * mm, "construction": true});
            skLineSegment(sketch, "E31", {"start": v(38.68, 7.38) * mm, "end": v(39.06, 9.5) * mm});
            skLineSegment(sketch, "E32", {"start": v(39.06, 9.5) * mm, "end": v(40.94, 9.5) * mm});
            skLineSegment(sketch, "E33.MirrorCS", {"start": v(41.32, 7.38) * mm, "end": v(40.94, 9.5) * mm});
            skLineSegment(sketch, "E34.1.0", {"start": v(36.72, 6.75) * mm, "end": v(35.18, 8.24) * mm});
            skLineSegment(sketch, "E34.1.1", {"start": v(33.65, 7.13) * mm, "end": v(35.18, 8.24) * mm});
            skLineSegment(sketch, "E34.1.2", {"start": v(34.6, 5.2) * mm, "end": v(33.65, 7.13) * mm});
            skLineSegment(sketch, "E34.2.0", {"start": v(33.38, 3.53) * mm, "end": v(31.26, 3.83) * mm});
            skLineSegment(sketch, "E34.2.1", {"start": v(30.67, 2.04) * mm, "end": v(31.26, 3.83) * mm});
            skLineSegment(sketch, "E34.2.2", {"start": v(32.57, 1.03) * mm, "end": v(30.67, 2.04) * mm});
            skLineSegment(sketch, "E35.1.3.0", {"start": v(32.57, -1.03) * mm, "end": v(30.67, -2.04) * mm});
            skLineSegment(sketch, "E35.3.3.0", {"start": v(31.26, -3.83) * mm, "end": v(30.67, -2.04) * mm});
            skLineSegment(sketch, "E35.6.3.0", {"start": v(33.38, -3.53) * mm, "end": v(31.26, -3.83) * mm});
            skLineSegment(sketch, "E35.1.4.0", {"start": v(34.6, -5.2) * mm, "end": v(33.65, -7.13) * mm});
            skLineSegment(sketch, "E35.3.4.0", {"start": v(35.18, -8.24) * mm, "end": v(33.65, -7.13) * mm});
            skLineSegment(sketch, "E35.6.4.0", {"start": v(36.72, -6.75) * mm, "end": v(35.18, -8.24) * mm});
            skLineSegment(sketch, "E35.1.5.0", {"start": v(38.68, -7.38) * mm, "end": v(39.06, -9.5) * mm});
            skLineSegment(sketch, "E35.3.5.0", {"start": v(40.94, -9.5) * mm, "end": v(39.06, -9.5) * mm});
            skLineSegment(sketch, "E35.6.5.0", {"start": v(41.32, -7.38) * mm, "end": v(40.94, -9.5) * mm});
            skLineSegment(sketch, "E35.1.6.0", {"start": v(43.28, -6.75) * mm, "end": v(44.82, -8.24) * mm});
            skLineSegment(sketch, "E35.3.6.0", {"start": v(46.35, -7.13) * mm, "end": v(44.82, -8.24) * mm});
            skLineSegment(sketch, "E35.6.6.0", {"start": v(45.4, -5.2) * mm, "end": v(46.35, -7.13) * mm});
            skLineSegment(sketch, "E35.1.7.0", {"start": v(46.62, -3.53) * mm, "end": v(48.74, -3.83) * mm});
            skLineSegment(sketch, "E35.3.7.0", {"start": v(49.33, -2.04) * mm, "end": v(48.74, -3.83) * mm});
            skLineSegment(sketch, "E35.6.7.0", {"start": v(47.43, -1.03) * mm, "end": v(49.33, -2.04) * mm});
            skLineSegment(sketch, "E35.1.8.0", {"start": v(47.43, 1.03) * mm, "end": v(49.33, 2.04) * mm});
            skLineSegment(sketch, "E35.3.8.0", {"start": v(48.74, 3.83) * mm, "end": v(49.33, 2.04) * mm});
            skLineSegment(sketch, "E35.6.8.0", {"start": v(46.62, 3.53) * mm, "end": v(48.74, 3.83) * mm});
            skLineSegment(sketch, "E35.1.9.0", {"start": v(45.4, 5.2) * mm, "end": v(46.35, 7.13) * mm});
            skLineSegment(sketch, "E35.3.9.0", {"start": v(44.82, 8.24) * mm, "end": v(46.35, 7.13) * mm});
            skLineSegment(sketch, "E35.6.9.0", {"start": v(43.28, 6.75) * mm, "end": v(44.82, 8.24) * mm});
            skSolve(sketch);
        }
        {
            var Q0;
            Q0 = qSketchRegion(id + "F16", true);
            extrude(context, id + "F17", {"entities" : qUnion([Q0]), "operationType" : NewBodyOperationType.ADD, "depth" : 4 * mm, "offsetDistance" : 25 * mm});
        }
        {
            var Q0;
            Q0=makeQuery(id+"F17.opExtrude","CAP_FACE",FACE,{"disambiguationData":[OSD([sQuery(id+"F16.wireOp",EDGE,"E29"),sQuery(id+"F16.wireOp",EDGE,"E31"),sQuery(id+"F16.wireOp",EDGE,"E32"),sQuery(id+"F16.wireOp",EDGE,"E33.MirrorCS"),sQuery(id+"F16.wireOp",EDGE,"E34.1.0"),sQuery(id+"F16.wireOp",EDGE,"E34.1.1"),sQuery(id+"F16.wireOp",EDGE,"E34.1.2"),sQuery(id+"F16.wireOp",EDGE,"E34.2.0"),sQuery(id+"F16.wireOp",EDGE,"E34.2.1"),sQuery(id+"F16.wireOp",EDGE,"E34.2.2"),sQuery(id+"F16.wireOp",EDGE,"E35.1.3.0"),sQuery(id+"F16.wireOp",EDGE,"E35.3.3.0"),sQuery(id+"F16.wireOp",EDGE,"E35.6.3.0"),sQuery(id+"F16.wireOp",EDGE,"E35.1.4.0"),sQuery(id+"F16.wireOp",EDGE,"E35.3.4.0"),sQuery(id+"F16.wireOp",EDGE,"E35.6.4.0"),sQuery(id+"F16.wireOp",EDGE,"E35.1.5.0"),sQuery(id+"F16.wireOp",EDGE,"E35.3.5.0"),sQuery(id+"F16.wireOp",EDGE,"E35.6.5.0"),sQuery(id+"F16.wireOp",EDGE,"E35.1.6.0"),sQuery(id+"F16.wireOp",EDGE,"E35.3.6.0"),sQuery(id+"F16.wireOp",EDGE,"E35.6.6.0"),sQuery(id+"F16.wireOp",EDGE,"E35.1.7.0"),sQuery(id+"F16.wireOp",EDGE,"E35.3.7.0"),sQuery(id+"F16.wireOp",EDGE,"E35.6.7.0"),sQuery(id+"F16.wireOp",EDGE,"E35.1.8.0"),sQuery(id+"F16.wireOp",EDGE,"E35.3.8.0"),sQuery(id+"F16.wireOp",EDGE,"E35.6.8.0"),sQuery(id+"F16.wireOp",EDGE,"E35.1.9.0"),sQuery(id+"F16.wireOp",EDGE,"E35.3.9.0"),sQuery(id+"F16.wireOp",EDGE,"E35.6.9.0")])],"isStart":false});
            var sketch = newSketch(context, id + "F18", { "sketchPlane" : qUnion([Q0])});
            skCircle(sketch, "E36.0", {"center": v(40, 0) * mm, "radius": 3 * mm});
            skSolve(sketch);
        }
        {
            var Q0;
            Q0 = qSketchRegion(id + "F18", true);
            extrude(context, id + "F19", {"entities" : qUnion([Q0]), "operationType" : NewBodyOperationType.ADD, "depth" : 2 * mm, "offsetDistance" : 25 * mm});
        }
        {
            var Q0;
            Q0=makeQuery(id+"F19.opExtrude","CAP_FACE",FACE,{"disambiguationData":[OSD([sQuery(id+"F18.wireOp",EDGE,"E36.0")])],"isStart":false});
            var sketch = newSketch(context, id + "F20", { "sketchPlane" : qUnion([Q0])});
            skLineSegment(sketch, "E37.bottom", {"start": v(-98, -98) * mm, "end": v(98, -98) * mm});
            skLineSegment(sketch, "E37.top", {"start": v(-98, 98) * mm, "end": v(98, 98) * mm});
            skLineSegment(sketch, "E37.left", {"start": v(-98, -98) * mm, "end": v(-98, 98) * mm});
            skLineSegment(sketch, "E37.right", {"start": v(98, -98) * mm, "end": v(98, 98) * mm});
            skPoint(sketch, "E37.middle", {"position": v(0, 0) * mm});
            skCircle(sketch, "E38.0", {"center": v(0, 0) * mm, "radius": 5 * mm});
            skSolve(sketch);
        }
        {
            var Q0;
            Q0 = qSketchRegion(id + "F20", true);
            extrude(context, id + "F21", {"entities" : qUnion([Q0]), "depth" : 1 * mm, "offsetDistance" : 25 * mm});
        }
        {
            var Q0;
            Q0=makeQuery(id+"F21.opExtrude","SWEPT_BODY",BODY,{"disambiguationData":[OSD([sQuery(id+"F20.wireOp",EDGE,"E37.bottom"),sQuery(id+"F20.wireOp",EDGE,"E37.top"),sQuery(id+"F20.wireOp",EDGE,"E37.left"),sQuery(id+"F20.wireOp",EDGE,"E37.right"),sQuery(id+"F20.wireOp",EDGE,"E38.0")])]});
            var Q1;
            Q1=makeQuery(id+"F1.opExtrude","SWEPT_BODY",BODY,{"disambiguationData":[OSD([sQuery(id+"F0.wireOp",EDGE,"E0.bottom"),sQuery(id+"F0.wireOp",EDGE,"E0.top"),sQuery(id+"F0.wireOp",EDGE,"E0.left"),sQuery(id+"F0.wireOp",EDGE,"E0.right")])]});
            booleanBodies(context, id + "F22", {"operationType" : BooleanOperationType.SUBTRACTION, "tools" : qUnion([Q0]), "targets" : qUnion([Q1]), "keepTools" : true});
        }
        {
            var Q0;
            Q0=makeQuery(id+"F21.opExtrude","CAP_FACE",FACE,{"disambiguationData":[OSD([sQuery(id+"F20.wireOp",EDGE,"E37.bottom"),sQuery(id+"F20.wireOp",EDGE,"E37.top"),sQuery(id+"F20.wireOp",EDGE,"E37.left"),sQuery(id+"F20.wireOp",EDGE,"E37.right"),sQuery(id+"F20.wireOp",EDGE,"E38.0")])],"isStart":true});
            var sketch = newSketch(context, id + "F23", { "sketchPlane" : qUnion([Q0])});
            skCircle(sketch, "E39.0", {"center": v(-40, 0) * mm, "radius": 3 * mm});
            skCircle(sketch, "E40", {"center": v(-40, 0) * mm, "radius": 5 * mm});
            skSolve(sketch);
        }
        {
            var Q0;
            Q0 = qSketchRegion(id + "F23", true);
            extrude(context, id + "F24", {"entities" : qUnion([Q0]), "operationType" : NewBodyOperationType.ADD, "endBound" : BoundingType.UP_TO_NEXT, "depth" : 25 * mm, "offsetDistance" : 25 * mm});
        }
        {
            var Q0;
            Q0=makeQuery(id+"F21.opExtrude","CAP_FACE",FACE,{"disambiguationData":[OSD([sQuery(id+"F20.wireOp",EDGE,"E37.bottom"),sQuery(id+"F20.wireOp",EDGE,"E37.top"),sQuery(id+"F20.wireOp",EDGE,"E37.left"),sQuery(id+"F20.wireOp",EDGE,"E37.right"),sQuery(id+"F20.wireOp",EDGE,"E38.0")])],"isStart":false});
            var sketch = newSketch(context, id + "F25", { "sketchPlane" : qUnion([Q0])});
            skText(sketch, "E41", { "text": "12", "fontName": "OpenSans-BoldItalic.ttf"});
            skText(sketch, "E42", { "text": "3", "fontName": "OpenSans-BoldItalic.ttf"});
            skText(sketch, "E43", { "text": "6", "fontName": "OpenSans-BoldItalic.ttf"});
            skText(sketch, "E44", { "text": "9", "fontName": "OpenSans-BoldItalic.ttf"});
            const initialGuessF25  = {"E41": [-0.015, 0.07, 1, 0, 0.01875], "E42": [0.07, -0.0125, 1, 0, 0.025], "E43": [-0.01125, -0.0908, 1, 0, 0.0258], "E44": [-0.08777, -0.0125, 1, 0, 0.025]};
            skSetInitialGuess(sketch, initialGuessF25);
            skSolve(sketch);
        }
        {
            var Q0;
            Q0 = qSketchRegion(id + "F25", true);
            extrude(context, id + "F26", {"entities" : qUnion([Q0]), "operationType" : NewBodyOperationType.REMOVE, "oppositeDirection" : true, "depth" : 0.5 * mm, "offsetDistance" : 25 * mm});
        }
        {
            var Q0;
            Q0=makeQuery(id+"F26.boolean.opBoolean","COPY",FACE,{"derivedFrom":makeQuery(id+"F26.opExtrude","CAP_FACE",FACE,{"disambiguationData":[OSD([sQuery(id+"F25.wireOp",EDGE,"E41.sketch_text.stroke-0"),sQuery(id+"F25.wireOp",EDGE,"E41.sketch_text.stroke-1"),sQuery(id+"F25.wireOp",EDGE,"E41.sketch_text.stroke-2"),sQuery(id+"F25.wireOp",EDGE,"E41.sketch_text.stroke-3"),sQuery(id+"F25.wireOp",EDGE,"E41.sketch_text.stroke-4"),sQuery(id+"F25.wireOp",EDGE,"E41.sketch_text.stroke-5"),sQuery(id+"F25.wireOp",EDGE,"E41.sketch_text.stroke-6"),sQuery(id+"F25.wireOp",EDGE,"E41.sketch_text.stroke-7"),sQuery(id+"F25.wireOp",EDGE,"E41.sketch_text.stroke-8")])],"isStart":false})});
            var Q1;
            Q1=makeQuery(id+"F26.boolean.opBoolean","COPY",FACE,{"derivedFrom":makeQuery(id+"F26.opExtrude","CAP_FACE",FACE,{"disambiguationData":[OSD([sQuery(id+"F25.wireOp",EDGE,"E41.sketch_text.stroke-9"),sQuery(id+"F25.wireOp",EDGE,"E41.sketch_text.stroke-10"),sQuery(id+"F25.wireOp",EDGE,"E41.sketch_text.stroke-11"),sQuery(id+"F25.wireOp",EDGE,"E41.sketch_text.stroke-12"),sQuery(id+"F25.wireOp",EDGE,"E41.sketch_text.stroke-13"),sQuery(id+"F25.wireOp",EDGE,"E41.sketch_text.stroke-14"),sQuery(id+"F25.wireOp",EDGE,"E41.sketch_text.stroke-15"),sQuery(id+"F25.wireOp",EDGE,"E41.sketch_text.stroke-16"),sQuery(id+"F25.wireOp",EDGE,"E41.sketch_text.stroke-17"),sQuery(id+"F25.wireOp",EDGE,"E41.sketch_text.stroke-18"),sQuery(id+"F25.wireOp",EDGE,"E41.sketch_text.stroke-19"),sQuery(id+"F25.wireOp",EDGE,"E41.sketch_text.stroke-20"),sQuery(id+"F25.wireOp",EDGE,"E41.sketch_text.stroke-21"),sQuery(id+"F25.wireOp",EDGE,"E41.sketch_text.stroke-22"),sQuery(id+"F25.wireOp",EDGE,"E41.sketch_text.stroke-23"),sQuery(id+"F25.wireOp",EDGE,"E41.sketch_text.stroke-24"),sQuery(id+"F25.wireOp",EDGE,"E41.sketch_text.stroke-25"),sQuery(id+"F25.wireOp",EDGE,"E41.sketch_text.stroke-26"),sQuery(id+"F25.wireOp",EDGE,"E41.sketch_text.stroke-27"),sQuery(id+"F25.wireOp",EDGE,"E41.sketch_text.stroke-28"),sQuery(id+"F25.wireOp",EDGE,"E41.sketch_text.stroke-29")])],"isStart":false})});
            var Q2;
            Q2=makeQuery(id+"F26.boolean.opBoolean","COPY",FACE,{"derivedFrom":makeQuery(id+"F26.opExtrude","CAP_FACE",FACE,{"disambiguationData":[OSD([sQuery(id+"F25.wireOp",EDGE,"E42.sketch_text.stroke-0"),sQuery(id+"F25.wireOp",EDGE,"E42.sketch_text.stroke-1"),sQuery(id+"F25.wireOp",EDGE,"E42.sketch_text.stroke-2"),sQuery(id+"F25.wireOp",EDGE,"E42.sketch_text.stroke-3"),sQuery(id+"F25.wireOp",EDGE,"E42.sketch_text.stroke-4"),sQuery(id+"F25.wireOp",EDGE,"E42.sketch_text.stroke-5"),sQuery(id+"F25.wireOp",EDGE,"E42.sketch_text.stroke-6"),sQuery(id+"F25.wireOp",EDGE,"E42.sketch_text.stroke-7"),sQuery(id+"F25.wireOp",EDGE,"E42.sketch_text.stroke-8"),sQuery(id+"F25.wireOp",EDGE,"E42.sketch_text.stroke-9"),sQuery(id+"F25.wireOp",EDGE,"E42.sketch_text.stroke-10"),sQuery(id+"F25.wireOp",EDGE,"E42.sketch_text.stroke-11"),sQuery(id+"F25.wireOp",EDGE,"E42.sketch_text.stroke-12"),sQuery(id+"F25.wireOp",EDGE,"E42.sketch_text.stroke-13"),sQuery(id+"F25.wireOp",EDGE,"E42.sketch_text.stroke-14"),sQuery(id+"F25.wireOp",EDGE,"E42.sketch_text.stroke-15"),sQuery(id+"F25.wireOp",EDGE,"E42.sketch_text.stroke-16"),sQuery(id+"F25.wireOp",EDGE,"E42.sketch_text.stroke-17"),sQuery(id+"F25.wireOp",EDGE,"E42.sketch_text.stroke-18"),sQuery(id+"F25.wireOp",EDGE,"E42.sketch_text.stroke-19"),sQuery(id+"F25.wireOp",EDGE,"E42.sketch_text.stroke-20"),sQuery(id+"F25.wireOp",EDGE,"E42.sketch_text.stroke-21"),sQuery(id+"F25.wireOp",EDGE,"E42.sketch_text.stroke-22"),sQuery(id+"F25.wireOp",EDGE,"E42.sketch_text.stroke-23"),sQuery(id+"F25.wireOp",EDGE,"E42.sketch_text.stroke-24"),sQuery(id+"F25.wireOp",EDGE,"E42.sketch_text.stroke-25"),sQuery(id+"F25.wireOp",EDGE,"E42.sketch_text.stroke-26"),sQuery(id+"F25.wireOp",EDGE,"E42.sketch_text.stroke-27")])],"isStart":false})});
            var Q3;
            Q3=makeQuery(id+"F26.boolean.opBoolean","COPY",FACE,{"derivedFrom":makeQuery(id+"F26.opExtrude","CAP_FACE",FACE,{"disambiguationData":[OSD([sQuery(id+"F25.wireOp",EDGE,"E43.sketch_text.stroke-0"),sQuery(id+"F25.wireOp",EDGE,"E43.sketch_text.stroke-1"),sQuery(id+"F25.wireOp",EDGE,"E43.sketch_text.stroke-2"),sQuery(id+"F25.wireOp",EDGE,"E43.sketch_text.stroke-3"),sQuery(id+"F25.wireOp",EDGE,"E43.sketch_text.stroke-4"),sQuery(id+"F25.wireOp",EDGE,"E43.sketch_text.stroke-5"),sQuery(id+"F25.wireOp",EDGE,"E43.sketch_text.stroke-6"),sQuery(id+"F25.wireOp",EDGE,"E43.sketch_text.stroke-7"),sQuery(id+"F25.wireOp",EDGE,"E43.sketch_text.stroke-8"),sQuery(id+"F25.wireOp",EDGE,"E43.sketch_text.stroke-9"),sQuery(id+"F25.wireOp",EDGE,"E43.sketch_text.stroke-10"),sQuery(id+"F25.wireOp",EDGE,"E43.sketch_text.stroke-11"),sQuery(id+"F25.wireOp",EDGE,"E43.sketch_text.stroke-12"),sQuery(id+"F25.wireOp",EDGE,"E43.sketch_text.stroke-13"),sQuery(id+"F25.wireOp",EDGE,"E43.sketch_text.stroke-14"),sQuery(id+"F25.wireOp",EDGE,"E43.sketch_text.stroke-15"),sQuery(id+"F25.wireOp",EDGE,"E43.sketch_text.stroke-16"),sQuery(id+"F25.wireOp",EDGE,"E43.sketch_text.stroke-17"),sQuery(id+"F25.wireOp",EDGE,"E43.sketch_text.stroke-18"),sQuery(id+"F25.wireOp",EDGE,"E43.sketch_text.stroke-19"),sQuery(id+"F25.wireOp",EDGE,"E43.sketch_text.stroke-20"),sQuery(id+"F25.wireOp",EDGE,"E43.sketch_text.stroke-21"),sQuery(id+"F25.wireOp",EDGE,"E43.sketch_text.stroke-22"),sQuery(id+"F25.wireOp",EDGE,"E43.sketch_text.stroke-23"),sQuery(id+"F25.wireOp",EDGE,"E43.sketch_text.stroke-24"),sQuery(id+"F25.wireOp",EDGE,"E43.sketch_text.stroke-25"),sQuery(id+"F25.wireOp",EDGE,"E43.sketch_text.stroke-26")])],"isStart":false})});
            var Q4;
            Q4=makeQuery(id+"F26.boolean.opBoolean","COPY",FACE,{"derivedFrom":makeQuery(id+"F26.opExtrude","CAP_FACE",FACE,{"disambiguationData":[OSD([sQuery(id+"F25.wireOp",EDGE,"E44.sketch_text.stroke-0"),sQuery(id+"F25.wireOp",EDGE,"E44.sketch_text.stroke-1"),sQuery(id+"F25.wireOp",EDGE,"E44.sketch_text.stroke-2"),sQuery(id+"F25.wireOp",EDGE,"E44.sketch_text.stroke-3"),sQuery(id+"F25.wireOp",EDGE,"E44.sketch_text.stroke-4"),sQuery(id+"F25.wireOp",EDGE,"E44.sketch_text.stroke-5"),sQuery(id+"F25.wireOp",EDGE,"E44.sketch_text.stroke-6"),sQuery(id+"F25.wireOp",EDGE,"E44.sketch_text.stroke-7"),sQuery(id+"F25.wireOp",EDGE,"E44.sketch_text.stroke-8"),sQuery(id+"F25.wireOp",EDGE,"E44.sketch_text.stroke-9"),sQuery(id+"F25.wireOp",EDGE,"E44.sketch_text.stroke-10"),sQuery(id+"F25.wireOp",EDGE,"E44.sketch_text.stroke-11"),sQuery(id+"F25.wireOp",EDGE,"E44.sketch_text.stroke-12"),sQuery(id+"F25.wireOp",EDGE,"E44.sketch_text.stroke-13"),sQuery(id+"F25.wireOp",EDGE,"E44.sketch_text.stroke-14"),sQuery(id+"F25.wireOp",EDGE,"E44.sketch_text.stroke-15"),sQuery(id+"F25.wireOp",EDGE,"E44.sketch_text.stroke-16"),sQuery(id+"F25.wireOp",EDGE,"E44.sketch_text.stroke-17"),sQuery(id+"F25.wireOp",EDGE,"E44.sketch_text.stroke-18"),sQuery(id+"F25.wireOp",EDGE,"E44.sketch_text.stroke-19"),sQuery(id+"F25.wireOp",EDGE,"E44.sketch_text.stroke-20"),sQuery(id+"F25.wireOp",EDGE,"E44.sketch_text.stroke-21"),sQuery(id+"F25.wireOp",EDGE,"E44.sketch_text.stroke-22"),sQuery(id+"F25.wireOp",EDGE,"E44.sketch_text.stroke-23"),sQuery(id+"F25.wireOp",EDGE,"E44.sketch_text.stroke-24"),sQuery(id+"F25.wireOp",EDGE,"E44.sketch_text.stroke-25"),sQuery(id+"F25.wireOp",EDGE,"E44.sketch_text.stroke-26"),sQuery(id+"F25.wireOp",EDGE,"E44.sketch_text.stroke-27")])],"isStart":false})});
            extrude(context, id + "F27", {"entities" : qUnion([Q0, Q1, Q2, Q3, Q4]), "depth" : 1 * mm, "offsetDistance" : 25 * mm});
        }
        {
            var Q0;
            Q0=makeQuery(id+"F15.opExtrude","CAP_FACE",FACE,{"disambiguationData":[OSD([sQuery(id+"F14.wireOp",EDGE,"E21.0"),sQuery(id+"F14.wireOp",EDGE,"E22"),sQuery(id+"F14.wireOp",EDGE,"E23"),sQuery(id+"F14.wireOp",EDGE,"E24"),sQuery(id+"F14.wireOp",EDGE,"E25.MirrorCS"),sQuery(id+"F14.wireOp",EDGE,"E26.MirrorCS"),sQuery(id+"F14.wireOp",EDGE,"E27.1.0"),sQuery(id+"F14.wireOp",EDGE,"E27.1.1"),sQuery(id+"F14.wireOp",EDGE,"E27.1.2"),sQuery(id+"F14.wireOp",EDGE,"E27.1.3"),sQuery(id+"F14.wireOp",EDGE,"E27.2.0"),sQuery(id+"F14.wireOp",EDGE,"E27.2.1"),sQuery(id+"F14.wireOp",EDGE,"E27.2.2"),sQuery(id+"F14.wireOp",EDGE,"E27.2.3"),sQuery(id+"F14.wireOp",EDGE,"E28.1.3.0"),sQuery(id+"F14.wireOp",EDGE,"E28.3.3.0"),sQuery(id+"F14.wireOp",EDGE,"E28.6.3.0"),sQuery(id+"F14.wireOp",EDGE,"E28.9.3.0"),sQuery(id+"F14.wireOp",EDGE,"E28.1.4.0"),sQuery(id+"F14.wireOp",EDGE,"E28.3.4.0"),sQuery(id+"F14.wireOp",EDGE,"E28.6.4.0"),sQuery(id+"F14.wireOp",EDGE,"E28.9.4.0"),sQuery(id+"F14.wireOp",EDGE,"E28.1.5.0"),sQuery(id+"F14.wireOp",EDGE,"E28.3.5.0"),sQuery(id+"F14.wireOp",EDGE,"E28.6.5.0"),sQuery(id+"F14.wireOp",EDGE,"E28.9.5.0"),sQuery(id+"F14.wireOp",EDGE,"E28.1.6.0"),sQuery(id+"F14.wireOp",EDGE,"E28.3.6.0"),sQuery(id+"F14.wireOp",EDGE,"E28.6.6.0"),sQuery(id+"F14.wireOp",EDGE,"E28.9.6.0"),sQuery(id+"F14.wireOp",EDGE,"E28.1.7.0"),sQuery(id+"F14.wireOp",EDGE,"E28.3.7.0"),sQuery(id+"F14.wireOp",EDGE,"E28.6.7.0"),sQuery(id+"F14.wireOp",EDGE,"E28.9.7.0"),sQuery(id+"F14.wireOp",EDGE,"E28.1.8.0"),sQuery(id+"F14.wireOp",EDGE,"E28.3.8.0"),sQuery(id+"F14.wireOp",EDGE,"E28.6.8.0"),sQuery(id+"F14.wireOp",EDGE,"E28.9.8.0"),sQuery(id+"F14.wireOp",EDGE,"E28.1.9.0"),sQuery(id+"F14.wireOp",EDGE,"E28.3.9.0"),sQuery(id+"F14.wireOp",EDGE,"E28.6.9.0"),sQuery(id+"F14.wireOp",EDGE,"E28.9.9.0"),sQuery(id+"F14.wireOp",EDGE,"E28.1.10.0"),sQuery(id+"F14.wireOp",EDGE,"E28.3.10.0"),sQuery(id+"F14.wireOp",EDGE,"E28.6.10.0"),sQuery(id+"F14.wireOp",EDGE,"E28.9.10.0"),sQuery(id+"F14.wireOp",EDGE,"E28.1.11.0"),sQuery(id+"F14.wireOp",EDGE,"E28.3.11.0"),sQuery(id+"F14.wireOp",EDGE,"E28.6.11.0"),sQuery(id+"F14.wireOp",EDGE,"E28.9.11.0"),sQuery(id+"F14.wireOp",EDGE,"E28.1.12.0"),sQuery(id+"F14.wireOp",EDGE,"E28.3.12.0"),sQuery(id+"F14.wireOp",EDGE,"E28.6.12.0"),sQuery(id+"F14.wireOp",EDGE,"E28.9.12.0"),sQuery(id+"F14.wireOp",EDGE,"E28.1.13.0"),sQuery(id+"F14.wireOp",EDGE,"E28.3.13.0"),sQuery(id+"F14.wireOp",EDGE,"E28.6.13.0"),sQuery(id+"F14.wireOp",EDGE,"E28.9.13.0"),sQuery(id+"F14.wireOp",EDGE,"E28.1.14.0"),sQuery(id+"F14.wireOp",EDGE,"E28.3.14.0"),sQuery(id+"F14.wireOp",EDGE,"E28.6.14.0"),sQuery(id+"F14.wireOp",EDGE,"E28.9.14.0"),sQuery(id+"F14.wireOp",EDGE,"E28.1.15.0"),sQuery(id+"F14.wireOp",EDGE,"E28.3.15.0"),sQuery(id+"F14.wireOp",EDGE,"E28.6.15.0"),sQuery(id+"F14.wireOp",EDGE,"E28.9.15.0"),sQuery(id+"F14.wireOp",EDGE,"E28.1.16.0"),sQuery(id+"F14.wireOp",EDGE,"E28.3.16.0"),sQuery(id+"F14.wireOp",EDGE,"E28.6.16.0"),sQuery(id+"F14.wireOp",EDGE,"E28.9.16.0"),sQuery(id+"F14.wireOp",EDGE,"E28.1.17.0"),sQuery(id+"F14.wireOp",EDGE,"E28.3.17.0"),sQuery(id+"F14.wireOp",EDGE,"E28.6.17.0"),sQuery(id+"F14.wireOp",EDGE,"E28.9.17.0"),sQuery(id+"F14.wireOp",EDGE,"E28.1.18.0"),sQuery(id+"F14.wireOp",EDGE,"E28.3.18.0"),sQuery(id+"F14.wireOp",EDGE,"E28.6.18.0"),sQuery(id+"F14.wireOp",EDGE,"E28.9.18.0"),sQuery(id+"F14.wireOp",EDGE,"E28.1.19.0"),sQuery(id+"F14.wireOp",EDGE,"E28.3.19.0"),sQuery(id+"F14.wireOp",EDGE,"E28.6.19.0"),sQuery(id+"F14.wireOp",EDGE,"E28.9.19.0"),sQuery(id+"F14.wireOp",EDGE,"E28.1.20.0"),sQuery(id+"F14.wireOp",EDGE,"E28.3.20.0"),sQuery(id+"F14.wireOp",EDGE,"E28.6.20.0"),sQuery(id+"F14.wireOp",EDGE,"E28.9.20.0"),sQuery(id+"F14.wireOp",EDGE,"E28.1.21.0"),sQuery(id+"F14.wireOp",EDGE,"E28.3.21.0"),sQuery(id+"F14.wireOp",EDGE,"E28.6.21.0"),sQuery(id+"F14.wireOp",EDGE,"E28.9.21.0"),sQuery(id+"F14.wireOp",EDGE,"E28.1.22.0"),sQuery(id+"F14.wireOp",EDGE,"E28.3.22.0"),sQuery(id+"F14.wireOp",EDGE,"E28.6.22.0"),sQuery(id+"F14.wireOp",EDGE,"E28.9.22.0"),sQuery(id+"F14.wireOp",EDGE,"E28.1.23.0"),sQuery(id+"F14.wireOp",EDGE,"E28.3.23.0"),sQuery(id+"F14.wireOp",EDGE,"E28.6.23.0"),sQuery(id+"F14.wireOp",EDGE,"E28.9.23.0"),sQuery(id+"F14.wireOp",EDGE,"E28.1.24.0"),sQuery(id+"F14.wireOp",EDGE,"E28.3.24.0"),sQuery(id+"F14.wireOp",EDGE,"E28.6.24.0"),sQuery(id+"F14.wireOp",EDGE,"E28.9.24.0"),sQuery(id+"F14.wireOp",EDGE,"E28.1.25.0"),sQuery(id+"F14.wireOp",EDGE,"E28.3.25.0"),sQuery(id+"F14.wireOp",EDGE,"E28.6.25.0"),sQuery(id+"F14.wireOp",EDGE,"E28.9.25.0"),sQuery(id+"F14.wireOp",EDGE,"E28.1.26.0"),sQuery(id+"F14.wireOp",EDGE,"E28.3.26.0"),sQuery(id+"F14.wireOp",EDGE,"E28.6.26.0"),sQuery(id+"F14.wireOp",EDGE,"E28.9.26.0"),sQuery(id+"F14.wireOp",EDGE,"E28.1.27.0"),sQuery(id+"F14.wireOp",EDGE,"E28.3.27.0"),sQuery(id+"F14.wireOp",EDGE,"E28.6.27.0"),sQuery(id+"F14.wireOp",EDGE,"E28.9.27.0"),sQuery(id+"F14.wireOp",EDGE,"E28.1.28.0"),sQuery(id+"F14.wireOp",EDGE,"E28.3.28.0"),sQuery(id+"F14.wireOp",EDGE,"E28.6.28.0"),sQuery(id+"F14.wireOp",EDGE,"E28.9.28.0"),sQuery(id+"F14.wireOp",EDGE,"E28.1.29.0"),sQuery(id+"F14.wireOp",EDGE,"E28.3.29.0"),sQuery(id+"F14.wireOp",EDGE,"E28.6.29.0"),sQuery(id+"F14.wireOp",EDGE,"E28.9.29.0"),sQuery(id+"F14.wireOp",EDGE,"E28.1.30.0"),sQuery(id+"F14.wireOp",EDGE,"E28.3.30.0"),sQuery(id+"F14.wireOp",EDGE,"E28.6.30.0"),sQuery(id+"F14.wireOp",EDGE,"E28.9.30.0"),sQuery(id+"F14.wireOp",EDGE,"E28.1.31.0"),sQuery(id+"F14.wireOp",EDGE,"E28.3.31.0"),sQuery(id+"F14.wireOp",EDGE,"E28.6.31.0"),sQuery(id+"F14.wireOp",EDGE,"E28.9.31.0"),sQuery(id+"F14.wireOp",EDGE,"E28.1.32.0"),sQuery(id+"F14.wireOp",EDGE,"E28.3.32.0"),sQuery(id+"F14.wireOp",EDGE,"E28.6.32.0"),sQuery(id+"F14.wireOp",EDGE,"E28.9.32.0"),sQuery(id+"F14.wireOp",EDGE,"E28.1.33.0"),sQuery(id+"F14.wireOp",EDGE,"E28.3.33.0"),sQuery(id+"F14.wireOp",EDGE,"E28.6.33.0"),sQuery(id+"F14.wireOp",EDGE,"E28.9.33.0"),sQuery(id+"F14.wireOp",EDGE,"E28.1.34.0"),sQuery(id+"F14.wireOp",EDGE,"E28.3.34.0"),sQuery(id+"F14.wireOp",EDGE,"E28.6.34.0"),sQuery(id+"F14.wireOp",EDGE,"E28.9.34.0"),sQuery(id+"F14.wireOp",EDGE,"E28.1.35.0"),sQuery(id+"F14.wireOp",EDGE,"E28.3.35.0"),sQuery(id+"F14.wireOp",EDGE,"E28.6.35.0"),sQuery(id+"F14.wireOp",EDGE,"E28.9.35.0"),sQuery(id+"F14.wireOp",EDGE,"E28.1.36.0"),sQuery(id+"F14.wireOp",EDGE,"E28.3.36.0"),sQuery(id+"F14.wireOp",EDGE,"E28.6.36.0"),sQuery(id+"F14.wireOp",EDGE,"E28.9.36.0"),sQuery(id+"F14.wireOp",EDGE,"E28.1.37.0"),sQuery(id+"F14.wireOp",EDGE,"E28.3.37.0"),sQuery(id+"F14.wireOp",EDGE,"E28.6.37.0"),sQuery(id+"F14.wireOp",EDGE,"E28.9.37.0"),sQuery(id+"F14.wireOp",EDGE,"E28.1.38.0"),sQuery(id+"F14.wireOp",EDGE,"E28.3.38.0"),sQuery(id+"F14.wireOp",EDGE,"E28.6.38.0"),sQuery(id+"F14.wireOp",EDGE,"E28.9.38.0"),sQuery(id+"F14.wireOp",EDGE,"E28.1.39.0"),sQuery(id+"F14.wireOp",EDGE,"E28.3.39.0"),sQuery(id+"F14.wireOp",EDGE,"E28.6.39.0"),sQuery(id+"F14.wireOp",EDGE,"E28.9.39.0")])],"isStart":false});
            var sketch = newSketch(context, id + "F28", { "sketchPlane" : qUnion([Q0])});
            skCircle(sketch, "E45.0", {"center": v(0, 0) * mm, "radius": 3 * mm});
            skCircle(sketch, "E46.0", {"center": v(0, 0) * mm, "radius": 5 * mm});
            skSolve(sketch);
        }
        {
            var Q0;
            Q0 = qSketchRegion(id + "F28", true);
            extrude(context, id + "F29", {"entities" : qUnion([Q0]), "operationType" : NewBodyOperationType.ADD, "depth" : 5 * mm, "offsetDistance" : 25 * mm});
        }
        {
            var Q0;
            Q0=makeQuery(id+"F29.opExtrude","CAP_FACE",FACE,{"disambiguationData":[OSD([sQuery(id+"F28.wireOp",EDGE,"E45.0"),sQuery(id+"F28.wireOp",EDGE,"E46.0")])],"isStart":false});
            var sketch = newSketch(context, id + "F30", { "sketchPlane" : qUnion([Q0])});
            skCircle(sketch, "E47.0", {"center": v(0, 0) * mm, "radius": 3 * mm});
            skCircle(sketch, "E48.0", {"center": v(0, 0) * mm, "radius": 5 * mm});
            skFitSpline(sketch, "E49", {"points": [v(1.07, 4.88) * mm, v(5.03, 10.77) * mm, v(1.54, 17.6) * mm, v(3.92, 23.95) * mm, v(1.86, 29.51) * mm, v(5.2, 36.98) * mm, v(0, 48.26) * mm], "startDerivative": vector(20.14, 26.8) * mm, "endDerivative": vector(-18.4, 33.22) * mm});
            skLineSegment(sketch, "E50", {"start": v(0, 0) * mm, "end": v(0, 8.77) * mm, "construction": true});
            skFitSpline(sketch, "E51.MirrorCS", {"points": [v(-1.07, 4.88) * mm, v(-5.03, 10.77) * mm, v(-1.54, 17.6) * mm, v(-3.92, 23.95) * mm, v(-1.86, 29.51) * mm, v(-5.2, 36.98) * mm, v(0, 48.26) * mm], "startDerivative": vector(-20.14, 26.8) * mm, "endDerivative": vector(18.4, 33.22) * mm});
            skSolve(sketch);
        }
        {
            var Q0;
            Q0 = qSketchRegion(id + "F30", true);
            extrude(context, id + "F31", {"entities" : qUnion([Q0]), "operationType" : NewBodyOperationType.ADD, "depth" : 1 * mm, "offsetDistance" : 25 * mm});
        }
        {
            var Q0;
            Q0=makeQuery(id+"F6.opExtrude","CAP_FACE",FACE,{"disambiguationData":[OSD([sQuery(id+"F0.wireOp",EDGE,"E0.bottom"),sQuery(id+"F0.wireOp",EDGE,"E0.top"),sQuery(id+"F0.wireOp",EDGE,"E0.left"),sQuery(id+"F0.wireOp",EDGE,"E0.right")])],"isStart":false});
            var sketch = newSketch(context, id + "F32", { "sketchPlane" : qUnion([Q0])});
            skCircle(sketch, "E52", {"center": v(0, 0) * mm, "radius": 3 * mm});
            skFitSpline(sketch, "E53", {"points": [v(1.4, 2.65) * mm, v(4.38, 5.85) * mm, v(1.9, 11.38) * mm, v(5.24, 17.28) * mm, v(2.17, 22.14) * mm, v(6, 28.85) * mm, v(2.5, 36.52) * mm, v(6.27, 45.15) * mm, v(1.79, 54.05) * mm, v(4.94, 60.87) * mm, v(2.53, 66.66) * mm], "startDerivative": vector(62.22, 47.08) * mm, "endDerivative": vector(-48.55, 48) * mm});
            skLineSegment(sketch, "E54", {"start": v(0, 0) * mm, "end": v(0, 72.14) * mm, "construction": true});
            skLineSegment(sketch, "E55", {"start": v(2.53, 66.66) * mm, "end": v(0, 72.14) * mm});
            skFitSpline(sketch, "E56", {"points": [v(-1.4, 2.65) * mm, v(-1.03, 5.75) * mm, v(-4.62, 11.38) * mm, v(-1.65, 17.28) * mm, v(-5.17, 22.14) * mm, v(-2.6, 28.85) * mm, v(-6.52, 36.52) * mm, v(-2, 45.15) * mm, v(-5.9, 54.05) * mm, v(-2.93, 60.87) * mm, v(-2.2, 66.66) * mm], "startDerivative": vector(25.84, 45.5) * mm, "endDerivative": vector(-13.34, 51.51) * mm});
            skLineSegment(sketch, "E57", {"start": v(0, 72.14) * mm, "end": v(-2.2, 66.66) * mm});
            skSolve(sketch);
        }
        {
            var Q0;
            Q0 = qSketchRegion(id + "F32", true);
            extrude(context, id + "F33", {"entities" : qUnion([Q0]), "operationType" : NewBodyOperationType.ADD, "depth" : 1 * mm, "offsetDistance" : 25 * mm});
        }
        {
            var Q0;
            Q0=makeQuery(id+"F1.opExtrude","CAP_FACE",FACE,{"disambiguationData":[OSD([sQuery(id+"F0.wireOp",EDGE,"E0.bottom"),sQuery(id+"F0.wireOp",EDGE,"E0.top"),sQuery(id+"F0.wireOp",EDGE,"E0.left"),sQuery(id+"F0.wireOp",EDGE,"E0.right")])],"isStart":true});
            var sketch = newSketch(context, id + "F34", { "sketchPlane" : qUnion([Q0])});
            skPoint(sketch, "E58.middle", {"position": v(0, 0) * mm});
            skCircle(sketch, "E59", {"center": v(0, 0) * mm, "radius": 25 * mm});
            skSolve(sketch);
        }
        {
            var Q0;
            Q0 = qSketchRegion(id + "F34", true);
            extrude(context, id + "F35", {"entities" : qUnion([Q0]), "operationType" : NewBodyOperationType.ADD, "depth" : 10 * mm, "offsetDistance" : 25 * mm});
        }
        {
            var Q0;
            Q0=makeQuery(id+"F35.opExtrude","CAP_FACE",FACE,{"disambiguationData":[OSD([sQuery(id+"F34.wireOp",EDGE,"E59")])],"isStart":false});
            var sketch = newSketch(context, id + "F36", { "sketchPlane" : qUnion([Q0])});
            skLineSegment(sketch, "E60.bottom", {"start": v(-0.75, 17) * mm, "end": v(0.75, 17) * mm});
            skLineSegment(sketch, "E60.top", {"start": v(-0.75, 23) * mm, "end": v(0.75, 23) * mm});
            skLineSegment(sketch, "E60.left", {"start": v(-0.75, 17) * mm, "end": v(-0.75, 23) * mm});
            skLineSegment(sketch, "E60.right", {"start": v(0.75, 17) * mm, "end": v(0.75, 23) * mm});
            skPoint(sketch, "E60.middle", {"position": v(0, 20) * mm});
            skLineSegment(sketch, "E61.1.0", {"start": v(-12.15, 19.54) * mm, "end": v(-10.85, 20.3) * mm});
            skLineSegment(sketch, "E61.1.1", {"start": v(-7.85, 15.1) * mm, "end": v(-10.85, 20.3) * mm});
            skLineSegment(sketch, "E61.1.2", {"start": v(-9.15, 14.35) * mm, "end": v(-12.15, 19.54) * mm});
            skLineSegment(sketch, "E61.1.3", {"start": v(-9.15, 14.35) * mm, "end": v(-7.85, 15.1) * mm});
            skLineSegment(sketch, "E61.2.0", {"start": v(-20.3, 10.85) * mm, "end": v(-19.54, 12.15) * mm});
            skLineSegment(sketch, "E61.2.1", {"start": v(-14.35, 9.15) * mm, "end": v(-19.54, 12.15) * mm});
            skLineSegment(sketch, "E61.2.2", {"start": v(-15.1, 7.85) * mm, "end": v(-20.3, 10.85) * mm});
            skLineSegment(sketch, "E61.2.3", {"start": v(-15.1, 7.85) * mm, "end": v(-14.35, 9.15) * mm});
            skPoint(sketch, "E61.center", {"position": v(0, 0) * mm});
            skLineSegment(sketch, "E62.1.3.0", {"start": v(-23, -0.75) * mm, "end": v(-23, 0.75) * mm});
            skLineSegment(sketch, "E62.3.3.0", {"start": v(-17, 0.75) * mm, "end": v(-23, 0.75) * mm});
            skLineSegment(sketch, "E62.6.3.0", {"start": v(-17, -0.75) * mm, "end": v(-23, -0.75) * mm});
            skLineSegment(sketch, "E62.9.3.0", {"start": v(-17, -0.75) * mm, "end": v(-17, 0.75) * mm});
            skLineSegment(sketch, "E62.1.4.0", {"start": v(-19.54, -12.15) * mm, "end": v(-20.3, -10.85) * mm});
            skLineSegment(sketch, "E62.3.4.0", {"start": v(-15.1, -7.85) * mm, "end": v(-20.3, -10.85) * mm});
            skLineSegment(sketch, "E62.6.4.0", {"start": v(-14.35, -9.15) * mm, "end": v(-19.54, -12.15) * mm});
            skLineSegment(sketch, "E62.9.4.0", {"start": v(-14.35, -9.15) * mm, "end": v(-15.1, -7.85) * mm});
            skLineSegment(sketch, "E62.1.5.0", {"start": v(-10.85, -20.3) * mm, "end": v(-12.15, -19.54) * mm});
            skLineSegment(sketch, "E62.3.5.0", {"start": v(-9.15, -14.35) * mm, "end": v(-12.15, -19.54) * mm});
            skLineSegment(sketch, "E62.6.5.0", {"start": v(-7.85, -15.1) * mm, "end": v(-10.85, -20.3) * mm});
            skLineSegment(sketch, "E62.9.5.0", {"start": v(-7.85, -15.1) * mm, "end": v(-9.15, -14.35) * mm});
            skLineSegment(sketch, "E62.1.6.0", {"start": v(0.75, -23) * mm, "end": v(-0.75, -23) * mm});
            skLineSegment(sketch, "E62.3.6.0", {"start": v(-0.75, -17) * mm, "end": v(-0.75, -23) * mm});
            skLineSegment(sketch, "E62.6.6.0", {"start": v(0.75, -17) * mm, "end": v(0.75, -23) * mm});
            skLineSegment(sketch, "E62.9.6.0", {"start": v(0.75, -17) * mm, "end": v(-0.75, -17) * mm});
            skLineSegment(sketch, "E62.1.7.0", {"start": v(12.15, -19.54) * mm, "end": v(10.85, -20.3) * mm});
            skLineSegment(sketch, "E62.3.7.0", {"start": v(7.85, -15.1) * mm, "end": v(10.85, -20.3) * mm});
            skLineSegment(sketch, "E62.6.7.0", {"start": v(9.15, -14.35) * mm, "end": v(12.15, -19.54) * mm});
            skLineSegment(sketch, "E62.9.7.0", {"start": v(9.15, -14.35) * mm, "end": v(7.85, -15.1) * mm});
            skLineSegment(sketch, "E62.1.8.0", {"start": v(20.3, -10.85) * mm, "end": v(19.54, -12.15) * mm});
            skLineSegment(sketch, "E62.3.8.0", {"start": v(14.35, -9.15) * mm, "end": v(19.54, -12.15) * mm});
            skLineSegment(sketch, "E62.6.8.0", {"start": v(15.1, -7.85) * mm, "end": v(20.3, -10.85) * mm});
            skLineSegment(sketch, "E62.9.8.0", {"start": v(15.1, -7.85) * mm, "end": v(14.35, -9.15) * mm});
            skLineSegment(sketch, "E62.1.9.0", {"start": v(23, 0.75) * mm, "end": v(23, -0.75) * mm});
            skLineSegment(sketch, "E62.3.9.0", {"start": v(17, -0.75) * mm, "end": v(23, -0.75) * mm});
            skLineSegment(sketch, "E62.6.9.0", {"start": v(17, 0.75) * mm, "end": v(23, 0.75) * mm});
            skLineSegment(sketch, "E62.9.9.0", {"start": v(17, 0.75) * mm, "end": v(17, -0.75) * mm});
            skLineSegment(sketch, "E63.1.10.0", {"start": v(19.54, 12.15) * mm, "end": v(20.3, 10.85) * mm});
            skLineSegment(sketch, "E63.3.10.0", {"start": v(15.1, 7.85) * mm, "end": v(20.3, 10.85) * mm});
            skLineSegment(sketch, "E63.6.10.0", {"start": v(14.35, 9.15) * mm, "end": v(19.54, 12.15) * mm});
            skLineSegment(sketch, "E63.9.10.0", {"start": v(14.35, 9.15) * mm, "end": v(15.1, 7.85) * mm});
            skLineSegment(sketch, "E63.1.11.0", {"start": v(10.85, 20.3) * mm, "end": v(12.15, 19.54) * mm});
            skLineSegment(sketch, "E63.3.11.0", {"start": v(9.15, 14.35) * mm, "end": v(12.15, 19.54) * mm});
            skLineSegment(sketch, "E63.6.11.0", {"start": v(7.85, 15.1) * mm, "end": v(10.85, 20.3) * mm});
            skLineSegment(sketch, "E63.9.11.0", {"start": v(7.85, 15.1) * mm, "end": v(9.15, 14.35) * mm});
            skSolve(sketch);
        }
        {
            var Q0;
            Q0 = qSketchRegion(id + "F36", true);
            extrude(context, id + "F37", {"entities" : qUnion([Q0]), "operationType" : NewBodyOperationType.REMOVE, "oppositeDirection" : true, "depth" : 0.5 * mm, "offsetDistance" : 25 * mm});
        }
        {
            var Q0;
            Q0=makeQuery(id+"F35.opExtrude","CAP_FACE",FACE,{"disambiguationData":[OSD([sQuery(id+"F34.wireOp",EDGE,"E59")])],"isStart":false});
            var sketch = newSketch(context, id + "F38", { "sketchPlane" : qUnion([Q0])});
            skCircle(sketch, "E64", {"center": v(0, 0) * mm, "radius": 3.75 * mm});
            skSolve(sketch);
        }
        {
            var Q0;
            Q0 = qSketchRegion(id + "F38", true);
            extrude(context, id + "F39", {"entities" : qUnion([Q0]), "endBound" : BoundingType.SYMMETRIC, "depth" : 10 * mm, "offsetDistance" : 25 * mm});
        }
        {
            var Q0;
            Q0=makeQuery(id+"F39.opExtrude","SWEPT_BODY",BODY,{"disambiguationData":[OSD([sQuery(id+"F38.wireOp",EDGE,"E64")])]});
            var Q1;
            Q1=makeQuery(id+"F1.opExtrude","SWEPT_BODY",BODY,{"disambiguationData":[OSD([sQuery(id+"F0.wireOp",EDGE,"E0.bottom"),sQuery(id+"F0.wireOp",EDGE,"E0.top"),sQuery(id+"F0.wireOp",EDGE,"E0.left"),sQuery(id+"F0.wireOp",EDGE,"E0.right")])]});
            booleanBodies(context, id + "F40", {"operationType" : BooleanOperationType.SUBTRACTION, "tools" : qUnion([Q0]), "targets" : qUnion([Q1]), "keepTools" : true});
        }
        {
            var Q0;
            Q0=makeQuery(id+"F39.opExtrude","CAP_FACE",FACE,{"disambiguationData":[OSD([sQuery(id+"F38.wireOp",EDGE,"E64")])],"isStart":false});
            cPlane(context, id + "F41", {"entities" : qUnion([Q0]), "cplaneType" : CPlaneType.OFFSET, "offset" : 2 * mm, "oppositeDirection" : true, "width" : 150 * mm, "height" : 150 * mm});
        }
        {
            var Q0;
            Q0=qCreatedBy(id+"F41.planeOp",FACE);
            var sketch = newSketch(context, id + "F42", { "sketchPlane" : qUnion([Q0])});
            skLineSegment(sketch, "E65", {"start": v(-0.5, 3.31) * mm, "end": v(-0.5, 7.06) * mm});
            skLineSegment(sketch, "E66", {"start": v(-0.5, 7.06) * mm, "end": v(0, 9) * mm});
            skLineSegment(sketch, "E67", {"start": v(-0.5, 3.31) * mm, "end": v(0, 3.31) * mm});
            skLineSegment(sketch, "E68.MirrorCS", {"start": v(0.5, 7.06) * mm, "end": v(0, 9) * mm});
            skLineSegment(sketch, "E69.MirrorCS", {"start": v(0.5, 3.31) * mm, "end": v(0.5, 7.06) * mm});
            skLineSegment(sketch, "E70.MirrorCS", {"start": v(0.5, 3.31) * mm, "end": v(0, 3.31) * mm});
            skLineSegment(sketch, "E71.1.0", {"start": v(-1.54, 2.97) * mm, "end": v(-3.75, 6) * mm});
            skLineSegment(sketch, "E71.1.1", {"start": v(-2.35, 2.39) * mm, "end": v(-4.56, 5.42) * mm});
            skLineSegment(sketch, "E71.1.2", {"start": v(-4.56, 5.42) * mm, "end": v(-5.3, 7.28) * mm});
            skLineSegment(sketch, "E71.1.3", {"start": v(-3.75, 6) * mm, "end": v(-5.3, 7.28) * mm});
            skLineSegment(sketch, "E71.1.4", {"start": v(-1.54, 2.97) * mm, "end": v(-1.95, 2.68) * mm});
            skLineSegment(sketch, "E71.1.5", {"start": v(-2.35, 2.39) * mm, "end": v(-1.95, 2.68) * mm});
            skLineSegment(sketch, "E71.2.0", {"start": v(-3, 1.5) * mm, "end": v(-6.56, 2.66) * mm});
            skLineSegment(sketch, "E71.2.1", {"start": v(-3.3, 0.55) * mm, "end": v(-6.87, 1.7) * mm});
            skLineSegment(sketch, "E71.2.2", {"start": v(-6.87, 1.7) * mm, "end": v(-8.56, 2.78) * mm});
            skLineSegment(sketch, "E71.2.3", {"start": v(-6.56, 2.66) * mm, "end": v(-8.56, 2.78) * mm});
            skLineSegment(sketch, "E71.2.4", {"start": v(-3, 1.5) * mm, "end": v(-3.15, 1.02) * mm});
            skLineSegment(sketch, "E71.2.5", {"start": v(-3.3, 0.55) * mm, "end": v(-3.15, 1.02) * mm});
            skPoint(sketch, "E71.center", {"position": v(0, 0) * mm});
            skLineSegment(sketch, "E72.1.3.0", {"start": v(-3.3, -0.55) * mm, "end": v(-6.87, -1.7) * mm});
            skLineSegment(sketch, "E72.3.3.0", {"start": v(-3, -1.5) * mm, "end": v(-6.56, -2.66) * mm});
            skLineSegment(sketch, "E72.6.3.0", {"start": v(-6.56, -2.66) * mm, "end": v(-8.56, -2.78) * mm});
            skLineSegment(sketch, "E72.9.3.0", {"start": v(-6.87, -1.7) * mm, "end": v(-8.56, -2.78) * mm});
            skLineSegment(sketch, "E72.12.3.0", {"start": v(-3.3, -0.55) * mm, "end": v(-3.15, -1.02) * mm});
            skLineSegment(sketch, "E72.15.3.0", {"start": v(-3, -1.5) * mm, "end": v(-3.15, -1.02) * mm});
            skLineSegment(sketch, "E72.1.4.0", {"start": v(-2.35, -2.39) * mm, "end": v(-4.56, -5.42) * mm});
            skLineSegment(sketch, "E72.3.4.0", {"start": v(-1.54, -2.97) * mm, "end": v(-3.75, -6) * mm});
            skLineSegment(sketch, "E72.6.4.0", {"start": v(-3.75, -6) * mm, "end": v(-5.3, -7.28) * mm});
            skLineSegment(sketch, "E72.9.4.0", {"start": v(-4.56, -5.42) * mm, "end": v(-5.3, -7.28) * mm});
            skLineSegment(sketch, "E72.12.4.0", {"start": v(-2.35, -2.39) * mm, "end": v(-1.95, -2.68) * mm});
            skLineSegment(sketch, "E72.15.4.0", {"start": v(-1.54, -2.97) * mm, "end": v(-1.95, -2.68) * mm});
            skLineSegment(sketch, "E72.1.5.0", {"start": v(-0.5, -3.31) * mm, "end": v(-0.5, -7.06) * mm});
            skLineSegment(sketch, "E72.3.5.0", {"start": v(0.5, -3.31) * mm, "end": v(0.5, -7.06) * mm});
            skLineSegment(sketch, "E72.6.5.0", {"start": v(0.5, -7.06) * mm, "end": v(0, -9) * mm});
            skLineSegment(sketch, "E72.9.5.0", {"start": v(-0.5, -7.06) * mm, "end": v(0, -9) * mm});
            skLineSegment(sketch, "E72.12.5.0", {"start": v(-0.5, -3.31) * mm, "end": v(0, -3.31) * mm});
            skLineSegment(sketch, "E72.15.5.0", {"start": v(0.5, -3.31) * mm, "end": v(0, -3.31) * mm});
            skLineSegment(sketch, "E72.1.6.0", {"start": v(1.54, -2.97) * mm, "end": v(3.75, -6) * mm});
            skLineSegment(sketch, "E72.3.6.0", {"start": v(2.35, -2.39) * mm, "end": v(4.56, -5.42) * mm});
            skLineSegment(sketch, "E72.6.6.0", {"start": v(4.56, -5.42) * mm, "end": v(5.3, -7.28) * mm});
            skLineSegment(sketch, "E72.9.6.0", {"start": v(3.75, -6) * mm, "end": v(5.3, -7.28) * mm});
            skLineSegment(sketch, "E72.12.6.0", {"start": v(1.54, -2.97) * mm, "end": v(1.95, -2.68) * mm});
            skLineSegment(sketch, "E72.15.6.0", {"start": v(2.35, -2.39) * mm, "end": v(1.95, -2.68) * mm});
            skLineSegment(sketch, "E72.1.7.0", {"start": v(3, -1.5) * mm, "end": v(6.56, -2.66) * mm});
            skLineSegment(sketch, "E72.3.7.0", {"start": v(3.3, -0.55) * mm, "end": v(6.87, -1.7) * mm});
            skLineSegment(sketch, "E72.6.7.0", {"start": v(6.87, -1.7) * mm, "end": v(8.56, -2.78) * mm});
            skLineSegment(sketch, "E72.9.7.0", {"start": v(6.56, -2.66) * mm, "end": v(8.56, -2.78) * mm});
            skLineSegment(sketch, "E72.12.7.0", {"start": v(3, -1.5) * mm, "end": v(3.15, -1.02) * mm});
            skLineSegment(sketch, "E72.15.7.0", {"start": v(3.3, -0.55) * mm, "end": v(3.15, -1.02) * mm});
            skLineSegment(sketch, "E72.1.8.0", {"start": v(3.3, 0.55) * mm, "end": v(6.87, 1.7) * mm});
            skLineSegment(sketch, "E72.3.8.0", {"start": v(3, 1.5) * mm, "end": v(6.56, 2.66) * mm});
            skLineSegment(sketch, "E72.6.8.0", {"start": v(6.56, 2.66) * mm, "end": v(8.56, 2.78) * mm});
            skLineSegment(sketch, "E72.9.8.0", {"start": v(6.87, 1.7) * mm, "end": v(8.56, 2.78) * mm});
            skLineSegment(sketch, "E72.12.8.0", {"start": v(3.3, 0.55) * mm, "end": v(3.15, 1.02) * mm});
            skLineSegment(sketch, "E72.15.8.0", {"start": v(3, 1.5) * mm, "end": v(3.15, 1.02) * mm});
            skLineSegment(sketch, "E72.1.9.0", {"start": v(2.35, 2.39) * mm, "end": v(4.56, 5.42) * mm});
            skLineSegment(sketch, "E72.3.9.0", {"start": v(1.54, 2.97) * mm, "end": v(3.75, 6) * mm});
            skLineSegment(sketch, "E72.6.9.0", {"start": v(3.75, 6) * mm, "end": v(5.3, 7.28) * mm});
            skLineSegment(sketch, "E72.9.9.0", {"start": v(4.56, 5.42) * mm, "end": v(5.3, 7.28) * mm});
            skLineSegment(sketch, "E72.12.9.0", {"start": v(2.35, 2.39) * mm, "end": v(1.95, 2.68) * mm});
            skLineSegment(sketch, "E72.15.9.0", {"start": v(1.54, 2.97) * mm, "end": v(1.95, 2.68) * mm});
            skSolve(sketch);
        }
        {
            var Q0;
            Q0 = qSketchRegion(id + "F42", true);
            extrude(context, id + "F43", {"entities" : qUnion([Q0]), "operationType" : NewBodyOperationType.REMOVE, "oppositeDirection" : true, "depth" : 1 * mm, "offsetDistance" : 25 * mm});
        }
        {
            var Q0;
            Q0=qCreatedBy(id+"F41.planeOp",FACE);
            var sketch = newSketch(context, id + "F44", { "sketchPlane" : qUnion([Q0])});
            skLineSegment(sketch, "E73.0", {"start": v(-0.5, 3.31) * mm, "end": v(0, 3.31) * mm});
            skLineSegment(sketch, "E74.0", {"start": v(0.5, 3.31) * mm, "end": v(0, 3.31) * mm});
            skLineSegment(sketch, "E75.0", {"start": v(0.5, 3.31) * mm, "end": v(0.5, 7.06) * mm});
            skLineSegment(sketch, "E76.0", {"start": v(-0.5, 3.31) * mm, "end": v(-0.5, 7.06) * mm});
            skLineSegment(sketch, "E77.0", {"start": v(-0.5, 7.06) * mm, "end": v(0, 9) * mm});
            skLineSegment(sketch, "E78.0", {"start": v(0.5, 7.06) * mm, "end": v(0, 9) * mm});
            skSolve(sketch);
        }
        {
            var Q0;
            Q0 = qSketchRegion(id + "F44", true);
            extrude(context, id + "F45", {"entities" : qUnion([Q0]), "oppositeDirection" : true, "depth" : 1 * mm, "offsetDistance" : 25 * mm});
        }
    });
